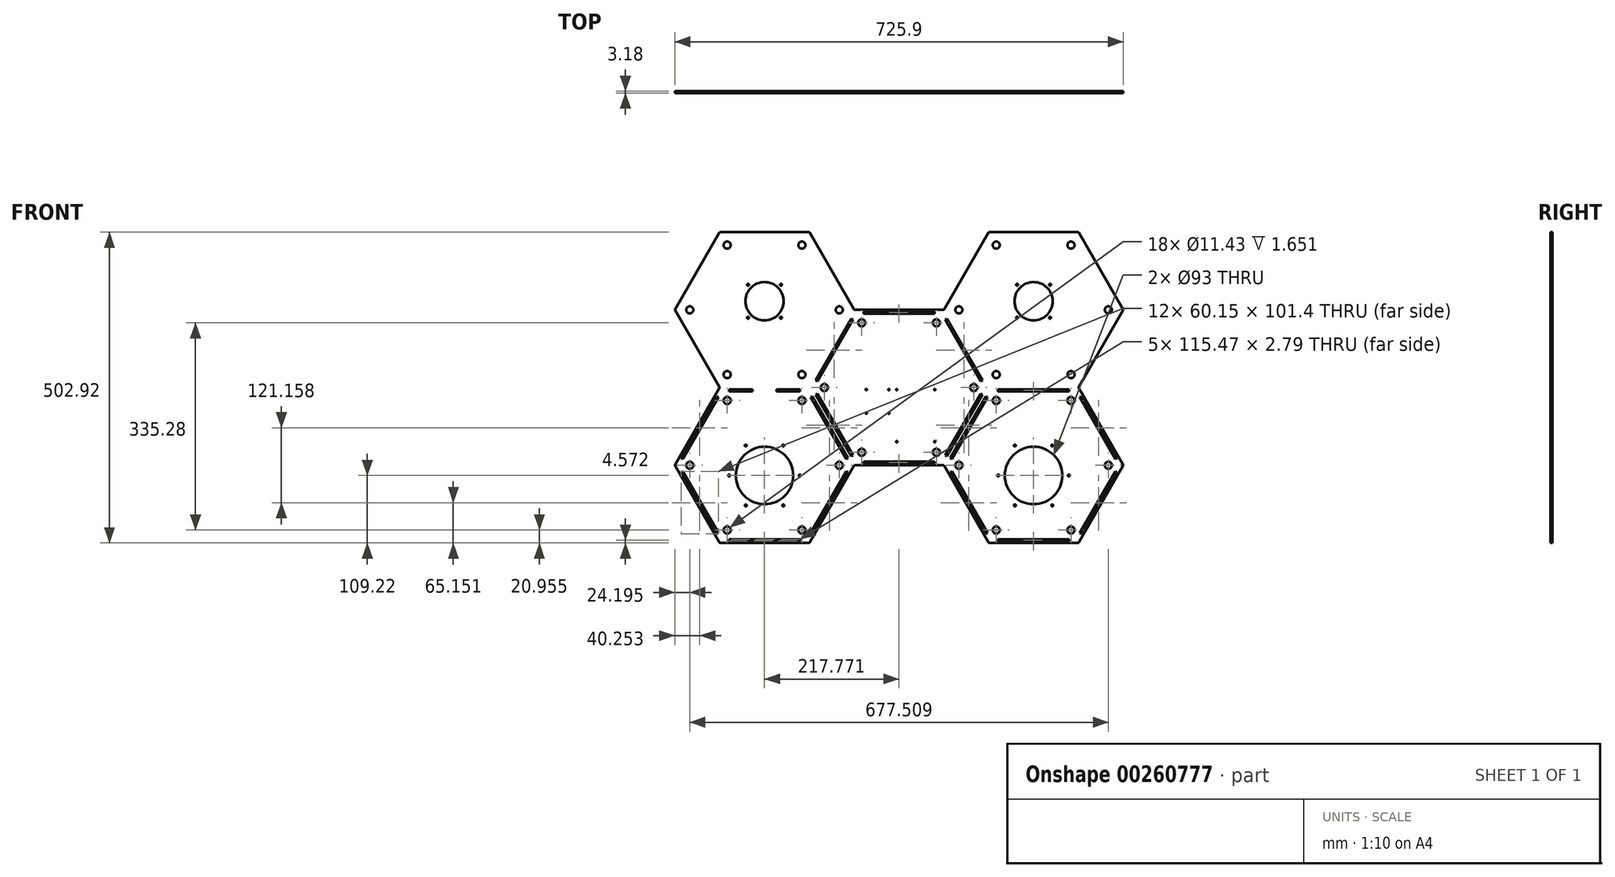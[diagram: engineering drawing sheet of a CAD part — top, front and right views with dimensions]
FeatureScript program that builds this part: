
annotation { "Feature Type Name" : "Feature", "Feature Type Description" : "" }
export const myFeature = defineFeature(function(context is Context, id is Id, definition is map)
    precondition{}
    {
        {
            var Q0;
            Q0=qCreatedBy(makeId("Front.planeOp"),FACE);
            var sketch = newSketch(context, id + "F0", { "sketchPlane" : qUnion([Q0])});
            skCircle(sketch, "E0.cCircle", {"center": v(0, 0) * mm, "radius": 125.73 * mm, "construction": true});
            skLineSegment(sketch, "E0.1", {"start": v(71.12, -125.73) * mm, "end": v(-71.12, -125.73) * mm});
            skLineSegment(sketch, "E0.4", {"start": v(-71.12, 125.73) * mm, "end": v(71.12, 125.73) * mm});
            skCircle(sketch, "E1.cCircle", {"center": v(-217.77, -125.73) * mm, "radius": 125.73 * mm, "construction": true});
            skLineSegment(sketch, "E1.0", {"start": v(-146.65, -251.46) * mm, "end": v(-288.9, -251.46) * mm});
            skLineSegment(sketch, "E1.1", {"start": v(-291.1, -250.19) * mm, "end": v(-362.22, -127) * mm});
            skLineSegment(sketch, "E1.2", {"start": v(-362.22, -124.46) * mm, "end": v(-291.1, -1.27) * mm});
            skLineSegment(sketch, "E1.5", {"start": v(-73.32, -127) * mm, "end": v(-144.45, -250.19) * mm});
            skPoint(sketch, "E1.0.midPoint", {"position": v(-217.77, -251.46) * mm});
            skCircle(sketch, "E2.cCircle", {"center": v(217.77, -125.73) * mm, "radius": 125.73 * mm, "construction": true});
            skLineSegment(sketch, "E2.0", {"start": v(362.22, -127) * mm, "end": v(291.1, -250.2) * mm});
            skLineSegment(sketch, "E2.1", {"start": v(288.9, -251.46) * mm, "end": v(146.65, -251.46) * mm});
            skLineSegment(sketch, "E2.2", {"start": v(144.45, -250.2) * mm, "end": v(73.32, -127) * mm});
            skLineSegment(sketch, "E2.5", {"start": v(291.1, -1.27) * mm, "end": v(362.22, -124.46) * mm});
            skPoint(sketch, "E2.0.midPoint", {"position": v(326.66, -188.6) * mm});
            skPoint(sketch, "E3.visualSharp", {"position": v(362.95, -125.73) * mm});
            skArc(sketch, "E3.filletArc", {"start": v(362.22, -127) * mm, "mid": v(362.56, -125.73) * mm, "end": v(362.22, -124.46) * mm});
            skPoint(sketch, "E4.visualSharp", {"position": v(290.36, -251.46) * mm});
            skArc(sketch, "E4.filletArc", {"start": v(288.9, -251.46) * mm, "mid": v(290.16, -251.12) * mm, "end": v(291.1, -250.2) * mm});
            skPoint(sketch, "E5.visualSharp", {"position": v(145.18, -251.46) * mm});
            skArc(sketch, "E5.filletArc", {"start": v(144.45, -250.2) * mm, "mid": v(145.38, -251.12) * mm, "end": v(146.65, -251.46) * mm});
            skPoint(sketch, "E6.visualSharp", {"position": v(72.6, -125.73) * mm});
            skArc(sketch, "E6.filletArc", {"start": v(73.32, -127) * mm, "mid": v(72.4, -126.07) * mm, "end": v(71.12, -125.73) * mm});
            skPoint(sketch, "E7.visualSharp", {"position": v(-72.6, -125.73) * mm});
            skArc(sketch, "E7.filletArc", {"start": v(-71.12, -125.73) * mm, "mid": v(-72.4, -126.07) * mm, "end": v(-73.32, -127) * mm});
            skPoint(sketch, "E8.visualSharp", {"position": v(-145.18, -251.46) * mm});
            skArc(sketch, "E8.filletArc", {"start": v(-146.65, -251.46) * mm, "mid": v(-145.38, -251.12) * mm, "end": v(-144.45, -250.19) * mm});
            skPoint(sketch, "E9.visualSharp", {"position": v(-290.36, -251.46) * mm});
            skArc(sketch, "E9.filletArc", {"start": v(-291.1, -250.19) * mm, "mid": v(-290.16, -251.12) * mm, "end": v(-288.9, -251.46) * mm});
            skPoint(sketch, "E10.visualSharp", {"position": v(-362.95, -125.73) * mm});
            skArc(sketch, "E10.filletArc", {"start": v(-362.22, -124.46) * mm, "mid": v(-362.56, -125.73) * mm, "end": v(-362.22, -127) * mm});
            skCircle(sketch, "E11.cCircle", {"center": v(-217.77, -125.73) * mm, "radius": 104.78 * mm, "construction": true});
            skLineSegment(sketch, "E11.0", {"start": v(-278.26, -20.95) * mm, "end": v(-157.28, -20.95) * mm, "construction": true});
            skLineSegment(sketch, "E11.1", {"start": v(-157.28, -20.95) * mm, "end": v(-96.79, -125.73) * mm, "construction": true});
            skLineSegment(sketch, "E11.2", {"start": v(-96.79, -125.73) * mm, "end": v(-157.28, -230.5) * mm, "construction": true});
            skLineSegment(sketch, "E11.3", {"start": v(-157.28, -230.5) * mm, "end": v(-278.26, -230.5) * mm, "construction": true});
            skLineSegment(sketch, "E11.4", {"start": v(-278.26, -230.5) * mm, "end": v(-338.75, -125.73) * mm, "construction": true});
            skLineSegment(sketch, "E11.5", {"start": v(-338.75, -125.73) * mm, "end": v(-278.26, -20.96) * mm, "construction": true});
            skPoint(sketch, "E11.0.midPoint", {"position": v(-217.77, -20.96) * mm});
            skCircle(sketch, "E12.cCircle", {"center": v(0, 0) * mm, "radius": 104.78 * mm, "construction": true});
            skLineSegment(sketch, "E12.0", {"start": v(60.5, 104.78) * mm, "end": v(120.98, 0) * mm, "construction": true});
            skLineSegment(sketch, "E12.1", {"start": v(120.98, 0) * mm, "end": v(60.5, -104.77) * mm, "construction": true});
            skLineSegment(sketch, "E12.2", {"start": v(60.5, -104.77) * mm, "end": v(-60.5, -104.78) * mm, "construction": true});
            skLineSegment(sketch, "E12.3", {"start": v(-60.5, -104.78) * mm, "end": v(-120.98, 0) * mm, "construction": true});
            skLineSegment(sketch, "E12.4", {"start": v(-120.98, 0) * mm, "end": v(-60.5, 104.78) * mm, "construction": true});
            skLineSegment(sketch, "E12.5", {"start": v(-60.5, 104.77) * mm, "end": v(60.5, 104.77) * mm, "construction": true});
            skPoint(sketch, "E12.0.midPoint", {"position": v(90.74, 52.39) * mm});
            skCircle(sketch, "E13.cCircle", {"center": v(217.77, -125.73) * mm, "radius": 104.78 * mm, "construction": true});
            skLineSegment(sketch, "E13.0", {"start": v(157.28, -20.96) * mm, "end": v(278.26, -20.96) * mm, "construction": true});
            skLineSegment(sketch, "E13.1", {"start": v(278.26, -20.96) * mm, "end": v(338.75, -125.73) * mm, "construction": true});
            skLineSegment(sketch, "E13.2", {"start": v(338.75, -125.73) * mm, "end": v(278.26, -230.5) * mm, "construction": true});
            skLineSegment(sketch, "E13.3", {"start": v(278.26, -230.5) * mm, "end": v(157.28, -230.5) * mm, "construction": true});
            skLineSegment(sketch, "E13.4", {"start": v(157.28, -230.5) * mm, "end": v(96.79, -125.73) * mm, "construction": true});
            skLineSegment(sketch, "E13.5", {"start": v(96.79, -125.73) * mm, "end": v(157.28, -20.96) * mm, "construction": true});
            skPoint(sketch, "E13.0.midPoint", {"position": v(217.77, -20.96) * mm});
            skCircle(sketch, "E14", {"center": v(-278.26, -20.96) * mm, "radius": 5.72 * mm});
            skCircle(sketch, "E15", {"center": v(-157.28, -20.95) * mm, "radius": 5.72 * mm});
            skCircle(sketch, "E16", {"center": v(-338.75, -125.73) * mm, "radius": 5.72 * mm});
            skCircle(sketch, "E17", {"center": v(-278.26, -230.5) * mm, "radius": 5.72 * mm});
            skCircle(sketch, "E18", {"center": v(-157.28, -230.5) * mm, "radius": 5.72 * mm});
            skCircle(sketch, "E19", {"center": v(-96.79, -125.73) * mm, "radius": 5.72 * mm});
            skCircle(sketch, "E20", {"center": v(-60.5, -104.78) * mm, "radius": 5.72 * mm});
            skCircle(sketch, "E21", {"center": v(-120.98, 0) * mm, "radius": 5.72 * mm});
            skCircle(sketch, "E22", {"center": v(-60.5, 104.77) * mm, "radius": 5.72 * mm});
            skCircle(sketch, "E23", {"center": v(60.5, 104.77) * mm, "radius": 5.72 * mm});
            skCircle(sketch, "E24", {"center": v(120.98, 0) * mm, "radius": 5.72 * mm});
            skCircle(sketch, "E25", {"center": v(60.5, -104.77) * mm, "radius": 5.72 * mm});
            skCircle(sketch, "E26", {"center": v(96.79, -125.73) * mm, "radius": 5.72 * mm});
            skCircle(sketch, "E27", {"center": v(157.28, -20.96) * mm, "radius": 5.72 * mm});
            skCircle(sketch, "E28", {"center": v(278.26, -20.96) * mm, "radius": 5.72 * mm});
            skCircle(sketch, "E29", {"center": v(338.75, -125.73) * mm, "radius": 5.72 * mm});
            skCircle(sketch, "E30", {"center": v(278.26, -230.5) * mm, "radius": 5.72 * mm});
            skCircle(sketch, "E31", {"center": v(157.28, -230.5) * mm, "radius": 5.72 * mm});
            skCircle(sketch, "E32.cCircle", {"center": v(-217.77, 125.73) * mm, "radius": 125.73 * mm, "construction": true});
            skLineSegment(sketch, "E32.0", {"start": v(-145.18, 251.46) * mm, "end": v(-73.32, 127) * mm});
            skLineSegment(sketch, "E32.3", {"start": v(-291.1, 1.27) * mm, "end": v(-362.95, 125.73) * mm});
            skLineSegment(sketch, "E32.4", {"start": v(-362.95, 125.73) * mm, "end": v(-290.36, 251.46) * mm});
            skLineSegment(sketch, "E32.5", {"start": v(-290.36, 251.46) * mm, "end": v(-145.18, 251.46) * mm});
            skPoint(sketch, "E32.0.midPoint", {"position": v(-108.89, 188.6) * mm});
            skCircle(sketch, "E33.cCircle", {"center": v(217.77, 125.73) * mm, "radius": 125.73 * mm, "construction": true});
            skLineSegment(sketch, "E33.0", {"start": v(290.36, 251.46) * mm, "end": v(362.95, 125.73) * mm});
            skLineSegment(sketch, "E33.1", {"start": v(362.95, 125.73) * mm, "end": v(291.1, 1.27) * mm});
            skLineSegment(sketch, "E33.4", {"start": v(73.32, 127) * mm, "end": v(145.18, 251.46) * mm});
            skLineSegment(sketch, "E33.5", {"start": v(145.18, 251.46) * mm, "end": v(290.36, 251.46) * mm});
            skPoint(sketch, "E33.0.midPoint", {"position": v(326.66, 188.6) * mm});
            skCircle(sketch, "E34.MirrorC", {"center": v(-278.26, 20.96) * mm, "radius": 5.72 * mm});
            skCircle(sketch, "E35.MirrorC", {"center": v(-157.28, 20.95) * mm, "radius": 5.72 * mm});
            skCircle(sketch, "E36.MirrorC", {"center": v(-338.75, 125.73) * mm, "radius": 5.72 * mm});
            skCircle(sketch, "E37.MirrorC", {"center": v(-278.26, 230.5) * mm, "radius": 5.72 * mm});
            skCircle(sketch, "E38.MirrorC", {"center": v(-157.28, 230.5) * mm, "radius": 5.72 * mm});
            skCircle(sketch, "E39.MirrorC", {"center": v(-96.79, 125.73) * mm, "radius": 5.72 * mm});
            skCircle(sketch, "E40.MirrorC", {"center": v(157.28, 20.96) * mm, "radius": 5.72 * mm});
            skCircle(sketch, "E41.MirrorC", {"center": v(278.26, 20.96) * mm, "radius": 5.72 * mm});
            skCircle(sketch, "E42.MirrorC", {"center": v(96.79, 125.73) * mm, "radius": 5.72 * mm});
            skCircle(sketch, "E43.MirrorC", {"center": v(338.75, 125.73) * mm, "radius": 5.72 * mm});
            skCircle(sketch, "E44.MirrorC", {"center": v(278.26, 230.5) * mm, "radius": 5.72 * mm});
            skCircle(sketch, "E45.MirrorC", {"center": v(157.28, 230.5) * mm, "radius": 5.72 * mm});
            skPoint(sketch, "E46.visualSharp", {"position": v(-290.36, 0) * mm});
            skArc(sketch, "E46.filletArc", {"start": v(-291.1, -1.27) * mm, "mid": v(-290.75, 0) * mm, "end": v(-291.1, 1.27) * mm});
            skPoint(sketch, "E47.visualSharp", {"position": v(290.36, 0) * mm});
            skArc(sketch, "E47.filletArc", {"start": v(291.1, 1.27) * mm, "mid": v(290.75, 0) * mm, "end": v(291.1, -1.27) * mm});
            skPoint(sketch, "E48.visualSharp", {"position": v(72.6, 125.73) * mm});
            skArc(sketch, "E48.filletArc", {"start": v(71.12, 125.73) * mm, "mid": v(72.4, 126.07) * mm, "end": v(73.32, 127) * mm});
            skPoint(sketch, "E49.visualSharp", {"position": v(-72.6, 125.73) * mm});
            skArc(sketch, "E49.filletArc", {"start": v(-73.32, 127) * mm, "mid": v(-72.4, 126.07) * mm, "end": v(-71.12, 125.73) * mm});
            skSolve(sketch);
        }
        {
            var Q0;
            Q0=makeQuery(id+"F0.imprint","IMPRINT",FACE,{"disambiguationData":[TD([[makeQuery(id+"F0.imprint","IMPRINT",EDGE,{"derivedFrom":sQuery(id+"F0.wireOp",EDGE,"E0.1")}),-1.0]])]});
            extrude(context, id + "F1", {"entities" : qUnion([Q0]), "depth" : 3.17 * mm});
        }
        {
            var Q0;
            Q0=makeQuery(id+"F0.imprint","IMPRINT",FACE,{"disambiguationData":[TD([[makeQuery(id+"F0.imprint","IMPRINT",EDGE,{"derivedFrom":sQuery(id+"F0.wireOp",EDGE,"E24")}),1.0]])]});
            var Q1;
            Q1=makeQuery(id+"F0.imprint","IMPRINT",FACE,{"disambiguationData":[TD([[makeQuery(id+"F0.imprint","IMPRINT",EDGE,{"derivedFrom":sQuery(id+"F0.wireOp",EDGE,"E27")}),1.0]])]});
            var Q2;
            Q2=makeQuery(id+"F0.imprint","IMPRINT",FACE,{"disambiguationData":[TD([[makeQuery(id+"F0.imprint","IMPRINT",EDGE,{"derivedFrom":sQuery(id+"F0.wireOp",EDGE,"E28")}),1.0]])]});
            var Q3;
            Q3=makeQuery(id+"F0.imprint","IMPRINT",FACE,{"disambiguationData":[TD([[makeQuery(id+"F0.imprint","IMPRINT",EDGE,{"derivedFrom":sQuery(id+"F0.wireOp",EDGE,"E29")}),1.0]])]});
            var Q4;
            Q4=makeQuery(id+"F0.imprint","IMPRINT",FACE,{"disambiguationData":[TD([[makeQuery(id+"F0.imprint","IMPRINT",EDGE,{"derivedFrom":sQuery(id+"F0.wireOp",EDGE,"E30")}),1.0]])]});
            var Q5;
            Q5=makeQuery(id+"F0.imprint","IMPRINT",FACE,{"disambiguationData":[TD([[makeQuery(id+"F0.imprint","IMPRINT",EDGE,{"derivedFrom":sQuery(id+"F0.wireOp",EDGE,"E31")}),1.0]])]});
            var Q6;
            Q6=makeQuery(id+"F0.imprint","IMPRINT",FACE,{"disambiguationData":[TD([[makeQuery(id+"F0.imprint","IMPRINT",EDGE,{"derivedFrom":sQuery(id+"F0.wireOp",EDGE,"E26")}),1.0]])]});
            var Q7;
            Q7=makeQuery(id+"F0.imprint","IMPRINT",FACE,{"disambiguationData":[TD([[makeQuery(id+"F0.imprint","IMPRINT",EDGE,{"derivedFrom":sQuery(id+"F0.wireOp",EDGE,"E25")}),1.0]])]});
            var Q8;
            Q8=makeQuery(id+"F0.imprint","IMPRINT",FACE,{"disambiguationData":[TD([[makeQuery(id+"F0.imprint","IMPRINT",EDGE,{"derivedFrom":sQuery(id+"F0.wireOp",EDGE,"E20")}),1.0]])]});
            var Q9;
            Q9=makeQuery(id+"F0.imprint","IMPRINT",FACE,{"disambiguationData":[TD([[makeQuery(id+"F0.imprint","IMPRINT",EDGE,{"derivedFrom":sQuery(id+"F0.wireOp",EDGE,"E19")}),1.0]])]});
            var Q10;
            Q10=makeQuery(id+"F0.imprint","IMPRINT",FACE,{"disambiguationData":[TD([[makeQuery(id+"F0.imprint","IMPRINT",EDGE,{"derivedFrom":sQuery(id+"F0.wireOp",EDGE,"E18")}),1.0]])]});
            var Q11;
            Q11=makeQuery(id+"F0.imprint","IMPRINT",FACE,{"disambiguationData":[TD([[makeQuery(id+"F0.imprint","IMPRINT",EDGE,{"derivedFrom":sQuery(id+"F0.wireOp",EDGE,"E17")}),1.0]])]});
            var Q12;
            Q12=makeQuery(id+"F0.imprint","IMPRINT",FACE,{"disambiguationData":[TD([[makeQuery(id+"F0.imprint","IMPRINT",EDGE,{"derivedFrom":sQuery(id+"F0.wireOp",EDGE,"E16")}),1.0]])]});
            var Q13;
            Q13=makeQuery(id+"F0.imprint","IMPRINT",FACE,{"disambiguationData":[TD([[makeQuery(id+"F0.imprint","IMPRINT",EDGE,{"derivedFrom":sQuery(id+"F0.wireOp",EDGE,"E14")}),1.0]])]});
            var Q14;
            Q14=makeQuery(id+"F0.imprint","IMPRINT",FACE,{"disambiguationData":[TD([[makeQuery(id+"F0.imprint","IMPRINT",EDGE,{"derivedFrom":sQuery(id+"F0.wireOp",EDGE,"E15")}),1.0]])]});
            var Q15;
            Q15=makeQuery(id+"F0.imprint","IMPRINT",FACE,{"disambiguationData":[TD([[makeQuery(id+"F0.imprint","IMPRINT",EDGE,{"derivedFrom":sQuery(id+"F0.wireOp",EDGE,"E21")}),1.0]])]});
            var Q16;
            Q16=makeQuery(id+"F0.imprint","IMPRINT",FACE,{"disambiguationData":[TD([[makeQuery(id+"F0.imprint","IMPRINT",EDGE,{"derivedFrom":sQuery(id+"F0.wireOp",EDGE,"E22")}),1.0]])]});
            var Q17;
            Q17=makeQuery(id+"F0.imprint","IMPRINT",FACE,{"disambiguationData":[TD([[makeQuery(id+"F0.imprint","IMPRINT",EDGE,{"derivedFrom":sQuery(id+"F0.wireOp",EDGE,"E23")}),1.0]])]});
            extrude(context, id + "F2", {"entities" : qUnion([Q0, Q1, Q2, Q3, Q4, Q5, Q6, Q7, Q8, Q9, Q10, Q11, Q12, Q13, Q14, Q15, Q16, Q17]), "operationType" : NewBodyOperationType.ADD, "depth" : 1.52 * mm});
        }
        {
            var Q0;
            Q0=makeQuery(id+"F1.opExtrude","CAP_FACE",FACE,{"disambiguationData":[OSD([sQuery(id+"F0.wireOp",EDGE,"E0.1"),sQuery(id+"F0.wireOp",EDGE,"E0.3"),sQuery(id+"F0.wireOp",EDGE,"E0.4"),sQuery(id+"F0.wireOp",EDGE,"E0.5"),sQuery(id+"F0.wireOp",EDGE,"E1.0"),sQuery(id+"F0.wireOp",EDGE,"E1.1"),sQuery(id+"F0.wireOp",EDGE,"E1.2"),sQuery(id+"F0.wireOp",EDGE,"E1.3"),sQuery(id+"F0.wireOp",EDGE,"E1.5"),sQuery(id+"F0.wireOp",EDGE,"E2.0"),sQuery(id+"F0.wireOp",EDGE,"E2.1"),sQuery(id+"F0.wireOp",EDGE,"E2.2"),sQuery(id+"F0.wireOp",EDGE,"E2.4"),sQuery(id+"F0.wireOp",EDGE,"E2.5"),sQuery(id+"F0.wireOp",EDGE,"d6ac2782-956d-471b-80da-3802cf03d7d4.filletArc"),sQuery(id+"F0.wireOp",EDGE,"c4cdf07e-024d-4eca-af19-9d9f9e97ded8.filletArc"),sQuery(id+"F0.wireOp",EDGE,"a3f6d1de-1ee9-4e34-8bae-e473824aa244.filletArc"),sQuery(id+"F0.wireOp",EDGE,"65f81674-14ca-4850-961e-3e155791f191.filletArc"),sQuery(id+"F0.wireOp",EDGE,"E3.filletArc"),sQuery(id+"F0.wireOp",EDGE,"E4.filletArc"),sQuery(id+"F0.wireOp",EDGE,"E5.filletArc"),sQuery(id+"F0.wireOp",EDGE,"E6.filletArc"),sQuery(id+"F0.wireOp",EDGE,"E7.filletArc"),sQuery(id+"F0.wireOp",EDGE,"E8.filletArc"),sQuery(id+"F0.wireOp",EDGE,"E9.filletArc"),sQuery(id+"F0.wireOp",EDGE,"E10.filletArc"),sQuery(id+"F0.wireOp",EDGE,"dc3c3065-ab0f-4737-a8f2-ea36e4ef4733.filletArc"),sQuery(id+"F0.wireOp",EDGE,"b4747763-c87b-4525-9a29-1839d3782590.filletArc"),sQuery(id+"F0.wireOp",EDGE,"E14"),sQuery(id+"F0.wireOp",EDGE,"E15"),sQuery(id+"F0.wireOp",EDGE,"E16"),sQuery(id+"F0.wireOp",EDGE,"E17"),sQuery(id+"F0.wireOp",EDGE,"E18"),sQuery(id+"F0.wireOp",EDGE,"E19"),sQuery(id+"F0.wireOp",EDGE,"E20"),sQuery(id+"F0.wireOp",EDGE,"E21"),sQuery(id+"F0.wireOp",EDGE,"E22"),sQuery(id+"F0.wireOp",EDGE,"E23"),sQuery(id+"F0.wireOp",EDGE,"E24"),sQuery(id+"F0.wireOp",EDGE,"E25"),sQuery(id+"F0.wireOp",EDGE,"E26"),sQuery(id+"F0.wireOp",EDGE,"E27"),sQuery(id+"F0.wireOp",EDGE,"E28"),sQuery(id+"F0.wireOp",EDGE,"E29"),sQuery(id+"F0.wireOp",EDGE,"E30"),sQuery(id+"F0.wireOp",EDGE,"E31")])],"isStart":false});
            var sketch = newSketch(context, id + "F3", { "sketchPlane" : qUnion([Q0])});
            skPoint(sketch, "E50", {"position": v(-217.77, -127) * mm});
            skCircle(sketch, "E51", {"center": v(-217.77, 139.7) * mm, "radius": 31 * mm});
            skCircle(sketch, "E52", {"center": v(-217.77, -142.24) * mm, "radius": 46.5 * mm});
            skLineSegment(sketch, "E53", {"start": v(-295.75, -142.24) * mm, "end": v(-133.33, -142.24) * mm, "construction": true});
            skCircle(sketch, "E54", {"center": v(-217.77, -142.24) * mm, "radius": 61.65 * mm, "construction": true});
            skCircle(sketch, "E55", {"center": v(-217.77, -142.24) * mm, "radius": 57.15 * mm, "construction": true});
            skCircle(sketch, "E56", {"center": v(-160.62, -142.24) * mm, "radius": 1.52 * mm});
            skLineSegment(sketch, "E57", {"start": v(-217.77, -142.24) * mm, "end": v(-217.77, 54.01) * mm, "construction": true});
            skLineSegment(sketch, "E58", {"start": v(-217.77, -142.24) * mm, "end": v(-187.49, -93.77) * mm, "construction": true});
            skLineSegment(sketch, "E59", {"start": v(-217.77, -142.24) * mm, "end": v(-187.49, -190.7) * mm, "construction": true});
            skCircle(sketch, "E60", {"center": v(-187.49, -93.77) * mm, "radius": 1.52 * mm});
            skCircle(sketch, "E61", {"center": v(-187.49, -190.7) * mm, "radius": 1.52 * mm});
            skCircle(sketch, "E62.MirrorC", {"center": v(-248.06, -93.77) * mm, "radius": 1.52 * mm});
            skCircle(sketch, "E63.MirrorC", {"center": v(-248.06, -190.7) * mm, "radius": 1.52 * mm});
            skCircle(sketch, "E64.MirrorC", {"center": v(-274.92, -142.24) * mm, "radius": 1.52 * mm});
            skCircle(sketch, "E65", {"center": v(-217.77, 139.7) * mm, "radius": 37.72 * mm, "construction": true});
            skLineSegment(sketch, "E66", {"start": v(-217.77, 139.7) * mm, "end": v(-244.44, 166.37) * mm, "construction": true});
            skCircle(sketch, "E67", {"center": v(-244.44, 166.37) * mm, "radius": 1.52 * mm});
            skCircle(sketch, "E68", {"center": v(-244.44, 113.03) * mm, "radius": 1.52 * mm});
            skCircle(sketch, "E69", {"center": v(-191.1, 113.03) * mm, "radius": 1.52 * mm});
            skCircle(sketch, "E70", {"center": v(-191.1, 166.37) * mm, "radius": 1.52 * mm});
            skLineSegment(sketch, "E71", {"start": v(-244.44, 166.37) * mm, "end": v(-191.1, 166.37) * mm, "construction": true});
            skCircle(sketch, "E72.MirrorC", {"center": v(160.62, -142.24) * mm, "radius": 1.52 * mm});
            skCircle(sketch, "E73.MirrorC", {"center": v(187.49, -190.7) * mm, "radius": 1.52 * mm});
            skCircle(sketch, "E74.MirrorC", {"center": v(248.06, -190.7) * mm, "radius": 1.52 * mm});
            skCircle(sketch, "E75.MirrorC", {"center": v(274.92, -142.24) * mm, "radius": 1.52 * mm});
            skCircle(sketch, "E76.MirrorC", {"center": v(187.49, -93.77) * mm, "radius": 1.52 * mm});
            skCircle(sketch, "E77.MirrorC", {"center": v(248.06, -93.77) * mm, "radius": 1.52 * mm});
            skCircle(sketch, "E78.MirrorC", {"center": v(217.77, -142.24) * mm, "radius": 46.5 * mm});
            skCircle(sketch, "E79.MirrorC", {"center": v(244.44, 113.03) * mm, "radius": 1.52 * mm});
            skCircle(sketch, "E80.MirrorC", {"center": v(191.1, 113.03) * mm, "radius": 1.52 * mm});
            skCircle(sketch, "E81.MirrorC", {"center": v(191.1, 166.37) * mm, "radius": 1.52 * mm});
            skCircle(sketch, "E82.MirrorC", {"center": v(217.77, 139.7) * mm, "radius": 31 * mm});
            skCircle(sketch, "E83.MirrorC", {"center": v(244.44, 166.37) * mm, "radius": 1.52 * mm});
            skSolve(sketch);
        }
        {
            var Q0;
            Q0=qSketchRegion(id+"F3",true);
            extrude(context, id + "F4", {"entities" : qUnion([Q0]), "operationType" : NewBodyOperationType.REMOVE, "endBound" : BoundingType.THROUGH_ALL, "oppositeDirection" : true, "depth" : 25.4 * mm});
        }
        {
            var Q0;
            Q0=makeQuery(id+"F1.opExtrude","CAP_FACE",FACE,{"disambiguationData":[OSD([sQuery(id+"F0.wireOp",EDGE,"E0.1"),sQuery(id+"F0.wireOp",EDGE,"E0.3"),sQuery(id+"F0.wireOp",EDGE,"E0.4"),sQuery(id+"F0.wireOp",EDGE,"E0.5"),sQuery(id+"F0.wireOp",EDGE,"E1.0"),sQuery(id+"F0.wireOp",EDGE,"E1.1"),sQuery(id+"F0.wireOp",EDGE,"E1.2"),sQuery(id+"F0.wireOp",EDGE,"E1.3"),sQuery(id+"F0.wireOp",EDGE,"E1.5"),sQuery(id+"F0.wireOp",EDGE,"E2.0"),sQuery(id+"F0.wireOp",EDGE,"E2.1"),sQuery(id+"F0.wireOp",EDGE,"E2.2"),sQuery(id+"F0.wireOp",EDGE,"E2.4"),sQuery(id+"F0.wireOp",EDGE,"E2.5"),sQuery(id+"F0.wireOp",EDGE,"d6ac2782-956d-471b-80da-3802cf03d7d4.filletArc"),sQuery(id+"F0.wireOp",EDGE,"c4cdf07e-024d-4eca-af19-9d9f9e97ded8.filletArc"),sQuery(id+"F0.wireOp",EDGE,"a3f6d1de-1ee9-4e34-8bae-e473824aa244.filletArc"),sQuery(id+"F0.wireOp",EDGE,"65f81674-14ca-4850-961e-3e155791f191.filletArc"),sQuery(id+"F0.wireOp",EDGE,"E3.filletArc"),sQuery(id+"F0.wireOp",EDGE,"E4.filletArc"),sQuery(id+"F0.wireOp",EDGE,"E5.filletArc"),sQuery(id+"F0.wireOp",EDGE,"E6.filletArc"),sQuery(id+"F0.wireOp",EDGE,"E7.filletArc"),sQuery(id+"F0.wireOp",EDGE,"E8.filletArc"),sQuery(id+"F0.wireOp",EDGE,"E9.filletArc"),sQuery(id+"F0.wireOp",EDGE,"E10.filletArc"),sQuery(id+"F0.wireOp",EDGE,"dc3c3065-ab0f-4737-a8f2-ea36e4ef4733.filletArc"),sQuery(id+"F0.wireOp",EDGE,"b4747763-c87b-4525-9a29-1839d3782590.filletArc"),sQuery(id+"F0.wireOp",EDGE,"E14"),sQuery(id+"F0.wireOp",EDGE,"E15"),sQuery(id+"F0.wireOp",EDGE,"E16"),sQuery(id+"F0.wireOp",EDGE,"E17"),sQuery(id+"F0.wireOp",EDGE,"E18"),sQuery(id+"F0.wireOp",EDGE,"E19"),sQuery(id+"F0.wireOp",EDGE,"E20"),sQuery(id+"F0.wireOp",EDGE,"E21"),sQuery(id+"F0.wireOp",EDGE,"E22"),sQuery(id+"F0.wireOp",EDGE,"E23"),sQuery(id+"F0.wireOp",EDGE,"E24"),sQuery(id+"F0.wireOp",EDGE,"E25"),sQuery(id+"F0.wireOp",EDGE,"E26"),sQuery(id+"F0.wireOp",EDGE,"E27"),sQuery(id+"F0.wireOp",EDGE,"E28"),sQuery(id+"F0.wireOp",EDGE,"E29"),sQuery(id+"F0.wireOp",EDGE,"E30"),sQuery(id+"F0.wireOp",EDGE,"E31")])],"isStart":false});
            var sketch = newSketch(context, id + "F5", { "sketchPlane" : qUnion([Q0])});
            skPoint(sketch, "E84", {"position": v(-217.77, -125.73) * mm});
            skCircle(sketch, "E85.cCircle", {"center": v(-217.77, -125.73) * mm, "radius": 125.73 * mm, "construction": true});
            skLineSegment(sketch, "E85.0", {"start": v(-275.7, 0) * mm, "end": v(-159.85, 0) * mm, "construction": true});
            skLineSegment(sketch, "E85.1", {"start": v(-137.85, -12.7) * mm, "end": v(-79.92, -113.03) * mm, "construction": true});
            skLineSegment(sketch, "E85.2", {"start": v(-79.92, -138.43) * mm, "end": v(-137.85, -238.76) * mm, "construction": true});
            skLineSegment(sketch, "E85.3", {"start": v(-159.85, -251.46) * mm, "end": v(-275.7, -251.46) * mm, "construction": true});
            skLineSegment(sketch, "E85.4", {"start": v(-297.7, -238.76) * mm, "end": v(-355.62, -138.43) * mm, "construction": true});
            skLineSegment(sketch, "E85.5", {"start": v(-355.62, -113.03) * mm, "end": v(-297.7, -12.7) * mm, "construction": true});
            skPoint(sketch, "E85.0.midPoint", {"position": v(-217.77, 0) * mm});
            skPoint(sketch, "E86.visualSharp", {"position": v(-290.36, 0) * mm});
            skArc(sketch, "E86.filletArc", {"start": v(-275.7, 0) * mm, "mid": v(-288.4, -3.4) * mm, "end": v(-297.7, -12.7) * mm, "construction": true});
            skPoint(sketch, "E87.visualSharp", {"position": v(-145.18, 0) * mm});
            skArc(sketch, "E87.filletArc", {"start": v(-137.85, -12.7) * mm, "mid": v(-147.15, -3.4) * mm, "end": v(-159.85, 0) * mm, "construction": true});
            skPoint(sketch, "E88.visualSharp", {"position": v(-72.6, -125.73) * mm});
            skArc(sketch, "E88.filletArc", {"start": v(-79.92, -138.43) * mm, "mid": v(-76.52, -125.73) * mm, "end": v(-79.92, -113.03) * mm, "construction": true});
            skPoint(sketch, "E89.visualSharp", {"position": v(-145.18, -251.46) * mm});
            skArc(sketch, "E89.filletArc", {"start": v(-159.85, -251.46) * mm, "mid": v(-147.15, -248.06) * mm, "end": v(-137.85, -238.76) * mm, "construction": true});
            skPoint(sketch, "E90.visualSharp", {"position": v(-290.36, -251.46) * mm});
            skArc(sketch, "E90.filletArc", {"start": v(-297.7, -238.76) * mm, "mid": v(-288.4, -248.06) * mm, "end": v(-275.7, -251.46) * mm, "construction": true});
            skPoint(sketch, "E91.visualSharp", {"position": v(-362.95, -125.73) * mm});
            skArc(sketch, "E91.filletArc", {"start": v(-355.62, -113.03) * mm, "mid": v(-359.02, -125.73) * mm, "end": v(-355.62, -138.43) * mm, "construction": true});
            skLineSegment(sketch, "E92.bottom", {"start": v(-275.5, -5.97) * mm, "end": v(-160.04, -5.97) * mm});
            skLineSegment(sketch, "E92.top", {"start": v(-275.5, -3.17) * mm, "end": v(-160.04, -3.17) * mm});
            skLineSegment(sketch, "E92.left", {"start": v(-275.5, -3.17) * mm, "end": v(-275.5, -5.97) * mm});
            skLineSegment(sketch, "E92.right", {"start": v(-160.04, -3.17) * mm, "end": v(-160.04, -5.97) * mm});
            skLineSegment(sketch, "E93.1.0", {"start": v(-352.77, -114.45) * mm, "end": v(-295.04, -14.45) * mm});
            skLineSegment(sketch, "E93.1.1", {"start": v(-352.77, -114.45) * mm, "end": v(-350.35, -115.85) * mm});
            skLineSegment(sketch, "E93.1.2", {"start": v(-350.35, -115.85) * mm, "end": v(-292.62, -15.85) * mm});
            skLineSegment(sketch, "E93.1.3", {"start": v(-295.04, -14.45) * mm, "end": v(-292.62, -15.85) * mm});
            skLineSegment(sketch, "E93.2.0", {"start": v(-295.04, -237) * mm, "end": v(-352.77, -137) * mm});
            skLineSegment(sketch, "E93.2.1", {"start": v(-295.04, -237) * mm, "end": v(-292.62, -235.61) * mm});
            skLineSegment(sketch, "E93.2.2", {"start": v(-292.62, -235.61) * mm, "end": v(-350.35, -135.61) * mm});
            skLineSegment(sketch, "E93.2.3", {"start": v(-352.77, -137) * mm, "end": v(-350.35, -135.61) * mm});
            skLineSegment(sketch, "E93.3.0", {"start": v(-160.04, -248.29) * mm, "end": v(-275.5, -248.29) * mm});
            skLineSegment(sketch, "E93.3.1", {"start": v(-160.04, -248.29) * mm, "end": v(-160.04, -245.5) * mm});
            skLineSegment(sketch, "E93.3.2", {"start": v(-160.04, -245.5) * mm, "end": v(-275.5, -245.5) * mm});
            skLineSegment(sketch, "E93.3.3", {"start": v(-275.5, -248.29) * mm, "end": v(-275.5, -245.5) * mm});
            skLineSegment(sketch, "E93.4.0", {"start": v(-82.77, -137) * mm, "end": v(-140.5, -237) * mm});
            skLineSegment(sketch, "E93.4.1", {"start": v(-82.77, -137) * mm, "end": v(-85.19, -135.61) * mm});
            skLineSegment(sketch, "E93.4.2", {"start": v(-85.19, -135.61) * mm, "end": v(-142.92, -235.61) * mm});
            skLineSegment(sketch, "E93.4.3", {"start": v(-140.5, -237) * mm, "end": v(-142.92, -235.61) * mm});
            skLineSegment(sketch, "E93.5.0", {"start": v(-140.5, -14.45) * mm, "end": v(-82.77, -114.45) * mm});
            skLineSegment(sketch, "E93.5.1", {"start": v(-140.5, -14.45) * mm, "end": v(-142.92, -15.85) * mm});
            skLineSegment(sketch, "E93.5.2", {"start": v(-142.92, -15.85) * mm, "end": v(-85.19, -115.85) * mm});
            skLineSegment(sketch, "E93.5.3", {"start": v(-82.77, -114.45) * mm, "end": v(-85.19, -115.85) * mm});
            skLineSegment(sketch, "E94.MirrorCS", {"start": v(140.5, -14.45) * mm, "end": v(142.92, -15.85) * mm});
            skLineSegment(sketch, "E95.MirrorCS", {"start": v(140.5, -14.45) * mm, "end": v(82.77, -114.45) * mm});
            skLineSegment(sketch, "E96.MirrorCS", {"start": v(142.92, -15.85) * mm, "end": v(85.19, -115.85) * mm});
            skLineSegment(sketch, "E97.MirrorCS", {"start": v(82.77, -114.45) * mm, "end": v(85.19, -115.85) * mm});
            skLineSegment(sketch, "E98.MirrorCS", {"start": v(82.77, -137) * mm, "end": v(85.19, -135.61) * mm});
            skLineSegment(sketch, "E99.MirrorCS", {"start": v(85.19, -135.61) * mm, "end": v(142.92, -235.61) * mm});
            skLineSegment(sketch, "E100.MirrorCS", {"start": v(82.77, -137) * mm, "end": v(140.5, -237) * mm});
            skLineSegment(sketch, "E101.MirrorCS", {"start": v(140.5, -237) * mm, "end": v(142.92, -235.61) * mm});
            skLineSegment(sketch, "E102.MirrorCS", {"start": v(160.04, -248.29) * mm, "end": v(160.04, -245.5) * mm});
            skLineSegment(sketch, "E103.MirrorCS", {"start": v(160.04, -248.29) * mm, "end": v(275.5, -248.29) * mm});
            skLineSegment(sketch, "E104.MirrorCS", {"start": v(160.04, -245.5) * mm, "end": v(275.5, -245.5) * mm});
            skLineSegment(sketch, "E105.MirrorCS", {"start": v(275.5, -248.29) * mm, "end": v(275.5, -245.5) * mm});
            skLineSegment(sketch, "E106.MirrorCS", {"start": v(295.04, -237) * mm, "end": v(292.62, -235.61) * mm});
            skLineSegment(sketch, "E107.MirrorCS", {"start": v(295.04, -237) * mm, "end": v(352.77, -137) * mm});
            skLineSegment(sketch, "E108.MirrorCS", {"start": v(292.62, -235.61) * mm, "end": v(350.35, -135.61) * mm});
            skLineSegment(sketch, "E109.MirrorCS", {"start": v(352.77, -137) * mm, "end": v(350.35, -135.61) * mm});
            skLineSegment(sketch, "E110.MirrorCS", {"start": v(352.77, -114.45) * mm, "end": v(350.35, -115.85) * mm});
            skLineSegment(sketch, "E111.MirrorCS", {"start": v(350.35, -115.85) * mm, "end": v(292.62, -15.85) * mm});
            skLineSegment(sketch, "E112.MirrorCS", {"start": v(352.77, -114.45) * mm, "end": v(295.04, -14.45) * mm});
            skLineSegment(sketch, "E113.MirrorCS", {"start": v(295.04, -14.45) * mm, "end": v(292.62, -15.85) * mm});
            skLineSegment(sketch, "E114.MirrorCS", {"start": v(275.5, -3.17) * mm, "end": v(275.5, -5.97) * mm});
            skLineSegment(sketch, "E115.MirrorCS", {"start": v(275.5, -5.97) * mm, "end": v(160.04, -5.97) * mm});
            skLineSegment(sketch, "E116.MirrorCS", {"start": v(275.5, -3.17) * mm, "end": v(160.04, -3.17) * mm});
            skLineSegment(sketch, "E117.MirrorCS", {"start": v(160.04, -3.17) * mm, "end": v(160.04, -5.97) * mm});
            skLineSegment(sketch, "E118.MirrorCS", {"start": v(57.74, -122.55) * mm, "end": v(57.74, -119.76) * mm});
            skLineSegment(sketch, "E119.MirrorCS", {"start": v(-57.74, -122.55) * mm, "end": v(57.74, -122.55) * mm});
            skLineSegment(sketch, "E120.MirrorCS", {"start": v(-57.74, -119.76) * mm, "end": v(57.74, -119.76) * mm});
            skLineSegment(sketch, "E121.MirrorCS", {"start": v(-57.74, -122.55) * mm, "end": v(-57.74, -119.76) * mm});
            skLineSegment(sketch, "E122.MirrorCS", {"start": v(-77.27, -111.28) * mm, "end": v(-74.85, -109.88) * mm});
            skLineSegment(sketch, "E123.MirrorCS", {"start": v(-132.58, -9.88) * mm, "end": v(-74.85, -109.88) * mm});
            skLineSegment(sketch, "E124.MirrorCS", {"start": v(-135, -11.28) * mm, "end": v(-77.27, -111.28) * mm});
            skLineSegment(sketch, "E125.MirrorCS", {"start": v(-135, -11.28) * mm, "end": v(-132.58, -9.88) * mm});
            skLineSegment(sketch, "E126.MirrorCS", {"start": v(-135, 11.28) * mm, "end": v(-132.58, 9.88) * mm});
            skLineSegment(sketch, "E127.MirrorCS", {"start": v(-74.85, 109.88) * mm, "end": v(-132.58, 9.88) * mm});
            skLineSegment(sketch, "E128.MirrorCS", {"start": v(-77.27, 111.28) * mm, "end": v(-135, 11.28) * mm});
            skLineSegment(sketch, "E129.MirrorCS", {"start": v(-77.27, 111.28) * mm, "end": v(-74.85, 109.88) * mm});
            skLineSegment(sketch, "E130.MirrorCS", {"start": v(-57.74, 122.56) * mm, "end": v(-57.74, 119.76) * mm});
            skLineSegment(sketch, "E131.MirrorCS", {"start": v(57.74, 119.76) * mm, "end": v(-57.74, 119.76) * mm});
            skLineSegment(sketch, "E132.MirrorCS", {"start": v(57.74, 122.56) * mm, "end": v(-57.74, 122.56) * mm});
            skLineSegment(sketch, "E133.MirrorCS", {"start": v(57.74, 122.56) * mm, "end": v(57.74, 119.76) * mm});
            skLineSegment(sketch, "E134.MirrorCS", {"start": v(77.27, 111.28) * mm, "end": v(74.85, 109.88) * mm});
            skLineSegment(sketch, "E135.MirrorCS", {"start": v(132.58, 9.88) * mm, "end": v(74.85, 109.88) * mm});
            skLineSegment(sketch, "E136.MirrorCS", {"start": v(135, 11.28) * mm, "end": v(77.27, 111.28) * mm});
            skLineSegment(sketch, "E137.MirrorCS", {"start": v(135, 11.28) * mm, "end": v(132.58, 9.88) * mm});
            skLineSegment(sketch, "E138.MirrorCS", {"start": v(135, -11.28) * mm, "end": v(132.58, -9.88) * mm});
            skLineSegment(sketch, "E139.MirrorCS", {"start": v(74.85, -109.88) * mm, "end": v(132.58, -9.88) * mm});
            skLineSegment(sketch, "E140.MirrorCS", {"start": v(77.27, -111.28) * mm, "end": v(74.85, -109.88) * mm});
            skLineSegment(sketch, "E141.MirrorCS", {"start": v(77.27, -111.28) * mm, "end": v(135, -11.28) * mm});
            skSolve(sketch);
        }
        {
            var Q0;
            Q0=qSketchRegion(id+"F5",true);
            extrude(context, id + "F6", {"entities" : qUnion([Q0]), "operationType" : NewBodyOperationType.REMOVE, "endBound" : BoundingType.THROUGH_ALL, "oppositeDirection" : true, "depth" : 25.4 * mm});
        }
        {
            var Q0;
            {var subQ0=sQuery(id+"F0.wireOp",EDGE,"E19");var subQ1=sQuery(id+"F0.wireOp",EDGE,"E14");var subQ2=sQuery(id+"F0.wireOp",EDGE,"E15");var subQ3=sQuery(id+"F0.wireOp",EDGE,"E16");var subQ4=sQuery(id+"F0.wireOp",EDGE,"E17");var subQ5=sQuery(id+"F0.wireOp",EDGE,"E18");Q0=makeQuery(id+"F0aKffUkCtTZm95_1.boolean.opBoolean","SPLIT",FACE,{"disambiguationData":[TD([makeQuery(id+"F1.opExtrude","SWEPT_FACE",FACE,{"disambiguationData":[OSD([subQ1])]})])],"derivedFrom":makeQuery(id+"F1.opExtrude","CAP_FACE",FACE,{"disambiguationData":[OSD([sQuery(id+"F0.wireOp",EDGE,"E0.1"),sQuery(id+"F0.wireOp",EDGE,"E0.3"),sQuery(id+"F0.wireOp",EDGE,"E0.4"),sQuery(id+"F0.wireOp",EDGE,"E0.5"),sQuery(id+"F0.wireOp",EDGE,"E1.0"),sQuery(id+"F0.wireOp",EDGE,"E1.1"),sQuery(id+"F0.wireOp",EDGE,"E1.2"),sQuery(id+"F0.wireOp",EDGE,"E1.3"),sQuery(id+"F0.wireOp",EDGE,"E1.5"),sQuery(id+"F0.wireOp",EDGE,"E2.0"),sQuery(id+"F0.wireOp",EDGE,"E2.1"),sQuery(id+"F0.wireOp",EDGE,"E2.2"),sQuery(id+"F0.wireOp",EDGE,"E2.4"),sQuery(id+"F0.wireOp",EDGE,"E2.5"),sQuery(id+"F0.wireOp",EDGE,"d6ac2782-956d-471b-80da-3802cf03d7d4.filletArc"),sQuery(id+"F0.wireOp",EDGE,"c4cdf07e-024d-4eca-af19-9d9f9e97ded8.filletArc"),sQuery(id+"F0.wireOp",EDGE,"a3f6d1de-1ee9-4e34-8bae-e473824aa244.filletArc"),sQuery(id+"F0.wireOp",EDGE,"65f81674-14ca-4850-961e-3e155791f191.filletArc"),sQuery(id+"F0.wireOp",EDGE,"E3.filletArc"),sQuery(id+"F0.wireOp",EDGE,"E4.filletArc"),sQuery(id+"F0.wireOp",EDGE,"E5.filletArc"),sQuery(id+"F0.wireOp",EDGE,"E6.filletArc"),sQuery(id+"F0.wireOp",EDGE,"E7.filletArc"),sQuery(id+"F0.wireOp",EDGE,"E8.filletArc"),sQuery(id+"F0.wireOp",EDGE,"E9.filletArc"),sQuery(id+"F0.wireOp",EDGE,"E10.filletArc"),sQuery(id+"F0.wireOp",EDGE,"dc3c3065-ab0f-4737-a8f2-ea36e4ef4733.filletArc"),sQuery(id+"F0.wireOp",EDGE,"b4747763-c87b-4525-9a29-1839d3782590.filletArc"),subQ1,subQ2,subQ3,subQ4,subQ5,subQ0,sQuery(id+"F0.wireOp",EDGE,"E20"),sQuery(id+"F0.wireOp",EDGE,"E21"),sQuery(id+"F0.wireOp",EDGE,"E22"),sQuery(id+"F0.wireOp",EDGE,"E23"),sQuery(id+"F0.wireOp",EDGE,"E24"),sQuery(id+"F0.wireOp",EDGE,"E25"),sQuery(id+"F0.wireOp",EDGE,"E26"),sQuery(id+"F0.wireOp",EDGE,"E27"),sQuery(id+"F0.wireOp",EDGE,"E28"),sQuery(id+"F0.wireOp",EDGE,"E29"),sQuery(id+"F0.wireOp",EDGE,"E30"),sQuery(id+"F0.wireOp",EDGE,"E31")])],"isStart":false})});}
            var sketch = newSketch(context, id + "F7", { "sketchPlane" : qUnion([Q0])});
            skLineSegment(sketch, "E142.bottom", {"start": v(-237.07, -5.97) * mm, "end": v(-198.47, -5.97) * mm});
            skLineSegment(sketch, "E142.top", {"start": v(-237.07, -3.17) * mm, "end": v(-198.47, -3.17) * mm});
            skLineSegment(sketch, "E142.left", {"start": v(-237.07, -5.97) * mm, "end": v(-237.07, -3.17) * mm});
            skLineSegment(sketch, "E142.right", {"start": v(-198.47, -5.97) * mm, "end": v(-198.47, -3.17) * mm});
            skPoint(sketch, "E143", {"position": v(-217.77, -5.97) * mm});
            skSolve(sketch);
        }
        {
            var Q0;
            Q0=qSketchRegion(id+"F7",true);
            var Q1;
            {var subQ0=sQuery(id+"F0.wireOp",EDGE,"E31");var subQ1=sQuery(id+"F0.wireOp",EDGE,"E30");var subQ2=sQuery(id+"F0.wireOp",EDGE,"E29");var subQ3=sQuery(id+"F0.wireOp",EDGE,"E28");var subQ4=sQuery(id+"F0.wireOp",EDGE,"E27");var subQ5=sQuery(id+"F0.wireOp",EDGE,"E26");var subQ6=sQuery(id+"F0.wireOp",EDGE,"E25");var subQ7=sQuery(id+"F0.wireOp",EDGE,"E24");var subQ8=sQuery(id+"F0.wireOp",EDGE,"E23");var subQ9=sQuery(id+"F0.wireOp",EDGE,"E22");var subQ10=sQuery(id+"F0.wireOp",EDGE,"E21");var subQ11=sQuery(id+"F0.wireOp",EDGE,"E20");var subQ12=sQuery(id+"F0.wireOp",EDGE,"E19");var subQ13=sQuery(id+"F0.wireOp",EDGE,"E18");var subQ14=sQuery(id+"F0.wireOp",EDGE,"E17");var subQ15=sQuery(id+"F0.wireOp",EDGE,"E16");var subQ16=sQuery(id+"F0.wireOp",EDGE,"E15");var subQ17=sQuery(id+"F0.wireOp",EDGE,"E14");Q1=makeQuery(id+"F2.boolean.opBoolean","MERGE",FACE,{"derivedFrom":[makeQuery(id+"F1.opExtrude","CAP_FACE",FACE,{"disambiguationData":[OSD([sQuery(id+"F0.wireOp",EDGE,"E0.1"),sQuery(id+"F0.wireOp",EDGE,"E0.3"),sQuery(id+"F0.wireOp",EDGE,"E0.4"),sQuery(id+"F0.wireOp",EDGE,"E0.5"),sQuery(id+"F0.wireOp",EDGE,"E1.0"),sQuery(id+"F0.wireOp",EDGE,"E1.1"),sQuery(id+"F0.wireOp",EDGE,"E1.2"),sQuery(id+"F0.wireOp",EDGE,"E1.3"),sQuery(id+"F0.wireOp",EDGE,"E1.5"),sQuery(id+"F0.wireOp",EDGE,"E2.0"),sQuery(id+"F0.wireOp",EDGE,"E2.1"),sQuery(id+"F0.wireOp",EDGE,"E2.2"),sQuery(id+"F0.wireOp",EDGE,"E2.4"),sQuery(id+"F0.wireOp",EDGE,"E2.5"),sQuery(id+"F0.wireOp",EDGE,"d6ac2782-956d-471b-80da-3802cf03d7d4.filletArc"),sQuery(id+"F0.wireOp",EDGE,"c4cdf07e-024d-4eca-af19-9d9f9e97ded8.filletArc"),sQuery(id+"F0.wireOp",EDGE,"a3f6d1de-1ee9-4e34-8bae-e473824aa244.filletArc"),sQuery(id+"F0.wireOp",EDGE,"65f81674-14ca-4850-961e-3e155791f191.filletArc"),sQuery(id+"F0.wireOp",EDGE,"E3.filletArc"),sQuery(id+"F0.wireOp",EDGE,"E4.filletArc"),sQuery(id+"F0.wireOp",EDGE,"E5.filletArc"),sQuery(id+"F0.wireOp",EDGE,"E6.filletArc"),sQuery(id+"F0.wireOp",EDGE,"E7.filletArc"),sQuery(id+"F0.wireOp",EDGE,"E8.filletArc"),sQuery(id+"F0.wireOp",EDGE,"E9.filletArc"),sQuery(id+"F0.wireOp",EDGE,"E10.filletArc"),sQuery(id+"F0.wireOp",EDGE,"dc3c3065-ab0f-4737-a8f2-ea36e4ef4733.filletArc"),sQuery(id+"F0.wireOp",EDGE,"b4747763-c87b-4525-9a29-1839d3782590.filletArc"),subQ17,subQ16,subQ15,subQ14,subQ13,subQ12,subQ11,subQ10,subQ9,subQ8,subQ7,subQ6,subQ5,subQ4,subQ3,subQ2,subQ1,subQ0])],"isStart":true}),makeQuery(id+"F2.opExtrude","CAP_FACE",FACE,{"disambiguationData":[OSD([subQ17])],"isStart":true}),makeQuery(id+"F2.opExtrude","CAP_FACE",FACE,{"disambiguationData":[OSD([subQ16])],"isStart":true}),makeQuery(id+"F2.opExtrude","CAP_FACE",FACE,{"disambiguationData":[OSD([subQ15])],"isStart":true}),makeQuery(id+"F2.opExtrude","CAP_FACE",FACE,{"disambiguationData":[OSD([subQ14])],"isStart":true}),makeQuery(id+"F2.opExtrude","CAP_FACE",FACE,{"disambiguationData":[OSD([subQ13])],"isStart":true}),makeQuery(id+"F2.opExtrude","CAP_FACE",FACE,{"disambiguationData":[OSD([subQ12])],"isStart":true}),makeQuery(id+"F2.opExtrude","CAP_FACE",FACE,{"disambiguationData":[OSD([subQ11])],"isStart":true}),makeQuery(id+"F2.opExtrude","CAP_FACE",FACE,{"disambiguationData":[OSD([subQ10])],"isStart":true}),makeQuery(id+"F2.opExtrude","CAP_FACE",FACE,{"disambiguationData":[OSD([subQ9])],"isStart":true}),makeQuery(id+"F2.opExtrude","CAP_FACE",FACE,{"disambiguationData":[OSD([subQ8])],"isStart":true}),makeQuery(id+"F2.opExtrude","CAP_FACE",FACE,{"disambiguationData":[OSD([subQ7])],"isStart":true}),makeQuery(id+"F2.opExtrude","CAP_FACE",FACE,{"disambiguationData":[OSD([subQ6])],"isStart":true}),makeQuery(id+"F2.opExtrude","CAP_FACE",FACE,{"disambiguationData":[OSD([subQ5])],"isStart":true}),makeQuery(id+"F2.opExtrude","CAP_FACE",FACE,{"disambiguationData":[OSD([subQ4])],"isStart":true}),makeQuery(id+"F2.opExtrude","CAP_FACE",FACE,{"disambiguationData":[OSD([subQ3])],"isStart":true}),makeQuery(id+"F2.opExtrude","CAP_FACE",FACE,{"disambiguationData":[OSD([subQ2])],"isStart":true}),makeQuery(id+"F2.opExtrude","CAP_FACE",FACE,{"disambiguationData":[OSD([subQ1])],"isStart":true}),makeQuery(id+"F2.opExtrude","CAP_FACE",FACE,{"disambiguationData":[OSD([subQ0])],"isStart":true})]});}
            extrude(context, id + "F8", {"entities" : qUnion([Q0]), "operationType" : NewBodyOperationType.ADD, "endBound" : BoundingType.UP_TO_SURFACE, "oppositeDirection" : true, "endBoundEntityFace" : qUnion([Q1]), "depth" : 25.4 * mm});
        }
        {
            var Q0;
            {var subQ0=sQuery(id+"F7.wireOp",EDGE,"E142.right");var subQ1=sQuery(id+"F7.wireOp",EDGE,"E142.left");var subQ2=sQuery(id+"F7.wireOp",EDGE,"E142.top");var subQ3=sQuery(id+"F7.wireOp",EDGE,"E142.bottom");var subQ4=sQuery(id+"F0.wireOp",EDGE,"E19");var subQ5=sQuery(id+"F0.wireOp",EDGE,"E14");var subQ6=sQuery(id+"F0.wireOp",EDGE,"E15");var subQ7=sQuery(id+"F0.wireOp",EDGE,"E16");var subQ8=sQuery(id+"F0.wireOp",EDGE,"E17");var subQ9=sQuery(id+"F0.wireOp",EDGE,"E18");var subQ10=sQuery(id+"F0.wireOp",EDGE,"E31");var subQ11=sQuery(id+"F0.wireOp",EDGE,"E30");var subQ12=sQuery(id+"F0.wireOp",EDGE,"E29");var subQ13=sQuery(id+"F0.wireOp",EDGE,"E28");var subQ14=sQuery(id+"F0.wireOp",EDGE,"E27");var subQ15=sQuery(id+"F0.wireOp",EDGE,"E26");var subQ16=sQuery(id+"F0.wireOp",EDGE,"E25");var subQ17=sQuery(id+"F0.wireOp",EDGE,"E24");var subQ18=sQuery(id+"F0.wireOp",EDGE,"E23");var subQ19=sQuery(id+"F0.wireOp",EDGE,"E22");var subQ20=sQuery(id+"F0.wireOp",EDGE,"E21");var subQ21=sQuery(id+"F0.wireOp",EDGE,"E20");var subQ22=sQuery(id+"F0.wireOp",EDGE,"b4747763-c87b-4525-9a29-1839d3782590.filletArc");var subQ23=sQuery(id+"F0.wireOp",EDGE,"dc3c3065-ab0f-4737-a8f2-ea36e4ef4733.filletArc");var subQ24=sQuery(id+"F0.wireOp",EDGE,"E10.filletArc");var subQ25=sQuery(id+"F0.wireOp",EDGE,"E9.filletArc");var subQ26=sQuery(id+"F0.wireOp",EDGE,"E8.filletArc");var subQ27=sQuery(id+"F0.wireOp",EDGE,"E7.filletArc");var subQ28=sQuery(id+"F0.wireOp",EDGE,"E6.filletArc");var subQ29=sQuery(id+"F0.wireOp",EDGE,"E5.filletArc");var subQ30=sQuery(id+"F0.wireOp",EDGE,"E4.filletArc");var subQ31=sQuery(id+"F0.wireOp",EDGE,"E3.filletArc");var subQ32=sQuery(id+"F0.wireOp",EDGE,"65f81674-14ca-4850-961e-3e155791f191.filletArc");var subQ33=sQuery(id+"F0.wireOp",EDGE,"a3f6d1de-1ee9-4e34-8bae-e473824aa244.filletArc");var subQ34=sQuery(id+"F0.wireOp",EDGE,"c4cdf07e-024d-4eca-af19-9d9f9e97ded8.filletArc");var subQ35=sQuery(id+"F0.wireOp",EDGE,"d6ac2782-956d-471b-80da-3802cf03d7d4.filletArc");var subQ36=sQuery(id+"F0.wireOp",EDGE,"E2.5");var subQ37=sQuery(id+"F0.wireOp",EDGE,"E2.4");var subQ38=sQuery(id+"F0.wireOp",EDGE,"E2.2");var subQ39=sQuery(id+"F0.wireOp",EDGE,"E2.1");var subQ40=sQuery(id+"F0.wireOp",EDGE,"E2.0");var subQ41=sQuery(id+"F0.wireOp",EDGE,"E1.5");var subQ42=sQuery(id+"F0.wireOp",EDGE,"E1.3");var subQ43=sQuery(id+"F0.wireOp",EDGE,"E1.2");var subQ44=sQuery(id+"F0.wireOp",EDGE,"E1.1");var subQ45=sQuery(id+"F0.wireOp",EDGE,"E1.0");var subQ46=sQuery(id+"F0.wireOp",EDGE,"E0.5");var subQ47=sQuery(id+"F0.wireOp",EDGE,"E0.4");var subQ48=sQuery(id+"F0.wireOp",EDGE,"E0.3");var subQ49=sQuery(id+"F0.wireOp",EDGE,"E0.1");var subQ50=makeQuery(id+"F1.opExtrude","CAP_FACE",FACE,{"disambiguationData":[OSD([subQ49,subQ48,subQ47,subQ46,subQ45,subQ44,subQ43,subQ42,subQ41,subQ40,subQ39,subQ38,subQ37,subQ36,subQ35,subQ34,subQ33,subQ32,subQ31,subQ30,subQ29,subQ28,subQ27,subQ26,subQ25,subQ24,subQ23,subQ22,subQ5,subQ6,subQ7,subQ8,subQ9,subQ4,subQ21,subQ20,subQ19,subQ18,subQ17,subQ16,subQ15,subQ14,subQ13,subQ12,subQ11,subQ10])],"isStart":false});Q0=makeQuery(id+"FArHMtP67R58qOK_1.1.FbB5umPfR1j8SLP_1.5.F8.boolean.opBoolean","MERGE",FACE,{"derivedFrom":[makeQuery(id+"FArHMtP67R58qOK_1.1.FbB5umPfR1j8SLP_1.4.F8.boolean.opBoolean","MERGE",FACE,{"derivedFrom":[makeQuery(id+"FArHMtP67R58qOK_1.1.FbB5umPfR1j8SLP_1.3.F8.boolean.opBoolean","MERGE",FACE,{"derivedFrom":[makeQuery(id+"FArHMtP67R58qOK_1.1.FbB5umPfR1j8SLP_1.2.F8.boolean.opBoolean","MERGE",FACE,{"derivedFrom":[makeQuery(id+"FArHMtP67R58qOK_1.1.FbB5umPfR1j8SLP_1.1.F8.boolean.opBoolean","MERGE",FACE,{"derivedFrom":[makeQuery(id+"FArHMtP67R58qOK_1.1.F8.boolean.opBoolean","MERGE",FACE,{"derivedFrom":[makeQuery(id+"F0aKffUkCtTZm95_1.boolean.opBoolean","SPLIT",FACE,{"disambiguationData":[TD([makeQuery(id+"F1.opExtrude","SWEPT_FACE",FACE,{"disambiguationData":[OSD([subQ21])]})])],"derivedFrom":subQ50}),makeQuery(id+"FZtU8A5xYbT4ezZ_1.1.FbB5umPfR1j8SLP_1.5.F8.boolean.opBoolean","MERGE",FACE,{"derivedFrom":[makeQuery(id+"FZtU8A5xYbT4ezZ_1.1.FbB5umPfR1j8SLP_1.4.F8.boolean.opBoolean","MERGE",FACE,{"derivedFrom":[makeQuery(id+"FZtU8A5xYbT4ezZ_1.1.FbB5umPfR1j8SLP_1.3.F8.boolean.opBoolean","MERGE",FACE,{"derivedFrom":[makeQuery(id+"FZtU8A5xYbT4ezZ_1.1.FbB5umPfR1j8SLP_1.2.F8.boolean.opBoolean","MERGE",FACE,{"derivedFrom":[makeQuery(id+"FZtU8A5xYbT4ezZ_1.1.FbB5umPfR1j8SLP_1.1.F8.boolean.opBoolean","MERGE",FACE,{"derivedFrom":[makeQuery(id+"FZtU8A5xYbT4ezZ_1.1.F8.boolean.opBoolean","MERGE",FACE,{"derivedFrom":[makeQuery(id+"F0aKffUkCtTZm95_1.boolean.opBoolean","SPLIT",FACE,{"disambiguationData":[TD([makeQuery(id+"F1.opExtrude","SWEPT_FACE",FACE,{"disambiguationData":[OSD([subQ15])]})])],"derivedFrom":subQ50}),makeQuery(id+"FbB5umPfR1j8SLP_1.5.F8.boolean.opBoolean","MERGE",FACE,{"derivedFrom":[makeQuery(id+"FbB5umPfR1j8SLP_1.4.F8.boolean.opBoolean","MERGE",FACE,{"derivedFrom":[makeQuery(id+"FbB5umPfR1j8SLP_1.3.F8.boolean.opBoolean","MERGE",FACE,{"derivedFrom":[makeQuery(id+"FbB5umPfR1j8SLP_1.2.F8.boolean.opBoolean","MERGE",FACE,{"derivedFrom":[makeQuery(id+"FbB5umPfR1j8SLP_1.1.F8.boolean.opBoolean","MERGE",FACE,{"derivedFrom":[makeQuery(id+"F8.boolean.opBoolean","MERGE",FACE,{"derivedFrom":[makeQuery(id+"F0aKffUkCtTZm95_1.boolean.opBoolean","SPLIT",FACE,{"disambiguationData":[TD([makeQuery(id+"F1.opExtrude","SWEPT_FACE",FACE,{"disambiguationData":[OSD([subQ49])]})])],"derivedFrom":subQ50}),makeQuery(id+"F0aKffUkCtTZm95_1.boolean.opBoolean","SPLIT",FACE,{"disambiguationData":[TD([makeQuery(id+"F1.opExtrude","SWEPT_FACE",FACE,{"disambiguationData":[OSD([subQ5])]})])],"derivedFrom":subQ50}),makeQuery(id+"F8.opExtrude","CAP_FACE",FACE,{"disambiguationData":[OSD([subQ3,subQ2,subQ1,subQ0])],"isStart":true})]}),makeQuery(id+"FbB5umPfR1j8SLP_1.1.F8.opExtrude","CAP_FACE",FACE,{"disambiguationData":[OSD([subQ3,subQ2,subQ1,subQ0])],"isStart":true})]}),makeQuery(id+"FbB5umPfR1j8SLP_1.2.F8.opExtrude","CAP_FACE",FACE,{"disambiguationData":[OSD([subQ3,subQ2,subQ1,subQ0])],"isStart":true})]}),makeQuery(id+"FbB5umPfR1j8SLP_1.3.F8.opExtrude","CAP_FACE",FACE,{"disambiguationData":[OSD([subQ3,subQ2,subQ1,subQ0])],"isStart":true})]}),makeQuery(id+"FbB5umPfR1j8SLP_1.4.F8.opExtrude","CAP_FACE",FACE,{"disambiguationData":[OSD([subQ3,subQ2,subQ1,subQ0])],"isStart":true})]}),makeQuery(id+"FbB5umPfR1j8SLP_1.5.F8.opExtrude","CAP_FACE",FACE,{"disambiguationData":[OSD([subQ3,subQ2,subQ1,subQ0])],"isStart":true})]}),makeQuery(id+"FZtU8A5xYbT4ezZ_1.1.F8.opExtrude","CAP_FACE",FACE,{"disambiguationData":[OSD([subQ3,subQ2,subQ1,subQ0])],"isStart":true})]}),makeQuery(id+"FZtU8A5xYbT4ezZ_1.1.FbB5umPfR1j8SLP_1.1.F8.opExtrude","CAP_FACE",FACE,{"disambiguationData":[OSD([subQ3,subQ2,subQ1,subQ0])],"isStart":true})]}),makeQuery(id+"FZtU8A5xYbT4ezZ_1.1.FbB5umPfR1j8SLP_1.2.F8.opExtrude","CAP_FACE",FACE,{"disambiguationData":[OSD([subQ3,subQ2,subQ1,subQ0])],"isStart":true})]}),makeQuery(id+"FZtU8A5xYbT4ezZ_1.1.FbB5umPfR1j8SLP_1.3.F8.opExtrude","CAP_FACE",FACE,{"disambiguationData":[OSD([subQ3,subQ2,subQ1,subQ0])],"isStart":true})]}),makeQuery(id+"FZtU8A5xYbT4ezZ_1.1.FbB5umPfR1j8SLP_1.4.F8.opExtrude","CAP_FACE",FACE,{"disambiguationData":[OSD([subQ3,subQ2,subQ1,subQ0])],"isStart":true})]}),makeQuery(id+"FZtU8A5xYbT4ezZ_1.1.FbB5umPfR1j8SLP_1.5.F8.opExtrude","CAP_FACE",FACE,{"disambiguationData":[OSD([subQ3,subQ2,subQ1,subQ0])],"isStart":true})]}),makeQuery(id+"FArHMtP67R58qOK_1.1.F8.opExtrude","CAP_FACE",FACE,{"disambiguationData":[OSD([subQ3,subQ2,subQ1,subQ0])],"isStart":true})]}),makeQuery(id+"FArHMtP67R58qOK_1.1.FbB5umPfR1j8SLP_1.1.F8.opExtrude","CAP_FACE",FACE,{"disambiguationData":[OSD([subQ3,subQ2,subQ1,subQ0])],"isStart":true})]}),makeQuery(id+"FArHMtP67R58qOK_1.1.FbB5umPfR1j8SLP_1.2.F8.opExtrude","CAP_FACE",FACE,{"disambiguationData":[OSD([subQ3,subQ2,subQ1,subQ0])],"isStart":true})]}),makeQuery(id+"FArHMtP67R58qOK_1.1.FbB5umPfR1j8SLP_1.3.F8.opExtrude","CAP_FACE",FACE,{"disambiguationData":[OSD([subQ3,subQ2,subQ1,subQ0])],"isStart":true})]}),makeQuery(id+"FArHMtP67R58qOK_1.1.FbB5umPfR1j8SLP_1.4.F8.opExtrude","CAP_FACE",FACE,{"disambiguationData":[OSD([subQ3,subQ2,subQ1,subQ0])],"isStart":true})]}),makeQuery(id+"FArHMtP67R58qOK_1.1.FbB5umPfR1j8SLP_1.5.F8.opExtrude","CAP_FACE",FACE,{"disambiguationData":[OSD([subQ3,subQ2,subQ1,subQ0])],"isStart":true})]});}
            var sketch = newSketch(context, id + "F9", { "sketchPlane" : qUnion([Q0])});
            skLineSegment(sketch, "E144.bottom", {"start": v(-3.73, -87.63) * mm, "end": v(57.74, -87.63) * mm, "construction": true});
            skLineSegment(sketch, "E144.top", {"start": v(-3.73, -3.3) * mm, "end": v(57.74, -3.3) * mm, "construction": true});
            skLineSegment(sketch, "E144.left", {"start": v(-3.73, -87.63) * mm, "end": v(-3.73, -3.3) * mm, "construction": true});
            skLineSegment(sketch, "E144.right", {"start": v(57.74, -87.63) * mm, "end": v(57.74, -3.3) * mm, "construction": true});
            skLineSegment(sketch, "E145.bottom", {"start": v(-53, -3.3) * mm, "end": v(-16.43, -3.3) * mm, "construction": true});
            skLineSegment(sketch, "E145.top", {"start": v(-53, -41.4) * mm, "end": v(-16.43, -41.4) * mm, "construction": true});
            skLineSegment(sketch, "E145.left", {"start": v(-53, -3.3) * mm, "end": v(-53, -41.4) * mm, "construction": true});
            skLineSegment(sketch, "E145.right", {"start": v(-16.43, -3.3) * mm, "end": v(-16.43, -41.4) * mm, "construction": true});
            skCircle(sketch, "E146", {"center": v(-53, -3.3) * mm, "radius": 1.14 * mm});
            skCircle(sketch, "E147", {"center": v(-16.43, -3.3) * mm, "radius": 1.14 * mm});
            skCircle(sketch, "E148", {"center": v(-53, -41.4) * mm, "radius": 1.14 * mm});
            skCircle(sketch, "E149", {"center": v(-3.73, -87.63) * mm, "radius": 1.14 * mm});
            skCircle(sketch, "E150", {"center": v(57.74, -87.63) * mm, "radius": 1.14 * mm});
            skCircle(sketch, "E151", {"center": v(57.74, -3.3) * mm, "radius": 1.14 * mm});
            skCircle(sketch, "E152", {"center": v(-3.73, -3.3) * mm, "radius": 1.14 * mm});
            skCircle(sketch, "E153", {"center": v(-16.43, -41.4) * mm, "radius": 1.14 * mm});
            skSolve(sketch);
        }
        {
            var Q0;
            Q0=qSketchRegion(id+"F9",true);
            var Q1;
            {var subQ0=sQuery(id+"F0.wireOp",EDGE,"E31");var subQ1=sQuery(id+"F0.wireOp",EDGE,"E30");var subQ2=sQuery(id+"F0.wireOp",EDGE,"E29");var subQ3=sQuery(id+"F0.wireOp",EDGE,"E28");var subQ4=sQuery(id+"F0.wireOp",EDGE,"E27");var subQ5=sQuery(id+"F0.wireOp",EDGE,"E26");var subQ6=sQuery(id+"F0.wireOp",EDGE,"E25");var subQ7=sQuery(id+"F0.wireOp",EDGE,"E24");var subQ8=sQuery(id+"F0.wireOp",EDGE,"E23");var subQ9=sQuery(id+"F0.wireOp",EDGE,"E22");var subQ10=sQuery(id+"F0.wireOp",EDGE,"E21");var subQ11=sQuery(id+"F0.wireOp",EDGE,"E20");var subQ12=sQuery(id+"F0.wireOp",EDGE,"E19");var subQ13=sQuery(id+"F0.wireOp",EDGE,"E18");var subQ14=sQuery(id+"F0.wireOp",EDGE,"E17");var subQ15=sQuery(id+"F0.wireOp",EDGE,"E16");var subQ16=sQuery(id+"F0.wireOp",EDGE,"E15");var subQ17=sQuery(id+"F0.wireOp",EDGE,"E14");var subQ18=sQuery(id+"F0.wireOp",EDGE,"b4747763-c87b-4525-9a29-1839d3782590.filletArc");var subQ19=sQuery(id+"F0.wireOp",EDGE,"dc3c3065-ab0f-4737-a8f2-ea36e4ef4733.filletArc");var subQ20=sQuery(id+"F0.wireOp",EDGE,"E10.filletArc");var subQ21=sQuery(id+"F0.wireOp",EDGE,"E9.filletArc");var subQ22=sQuery(id+"F0.wireOp",EDGE,"E8.filletArc");var subQ23=sQuery(id+"F0.wireOp",EDGE,"E7.filletArc");var subQ24=sQuery(id+"F0.wireOp",EDGE,"E6.filletArc");var subQ25=sQuery(id+"F0.wireOp",EDGE,"E5.filletArc");var subQ26=sQuery(id+"F0.wireOp",EDGE,"E4.filletArc");var subQ27=sQuery(id+"F0.wireOp",EDGE,"E3.filletArc");var subQ28=sQuery(id+"F0.wireOp",EDGE,"65f81674-14ca-4850-961e-3e155791f191.filletArc");var subQ29=sQuery(id+"F0.wireOp",EDGE,"a3f6d1de-1ee9-4e34-8bae-e473824aa244.filletArc");var subQ30=sQuery(id+"F0.wireOp",EDGE,"c4cdf07e-024d-4eca-af19-9d9f9e97ded8.filletArc");var subQ31=sQuery(id+"F0.wireOp",EDGE,"d6ac2782-956d-471b-80da-3802cf03d7d4.filletArc");var subQ32=sQuery(id+"F0.wireOp",EDGE,"E2.5");var subQ33=sQuery(id+"F0.wireOp",EDGE,"E2.4");var subQ34=sQuery(id+"F0.wireOp",EDGE,"E2.2");var subQ35=sQuery(id+"F0.wireOp",EDGE,"E2.1");var subQ36=sQuery(id+"F0.wireOp",EDGE,"E2.0");var subQ37=sQuery(id+"F0.wireOp",EDGE,"E1.5");var subQ38=sQuery(id+"F0.wireOp",EDGE,"E1.3");var subQ39=sQuery(id+"F0.wireOp",EDGE,"E1.2");var subQ40=sQuery(id+"F0.wireOp",EDGE,"E1.1");var subQ41=sQuery(id+"F0.wireOp",EDGE,"E1.0");var subQ42=sQuery(id+"F0.wireOp",EDGE,"E0.5");var subQ43=sQuery(id+"F0.wireOp",EDGE,"E0.4");var subQ44=sQuery(id+"F0.wireOp",EDGE,"E0.3");var subQ45=sQuery(id+"F0.wireOp",EDGE,"E0.1");Q1=makeQuery(id+"FArHMtP67R58qOK_1.1.FbB5umPfR1j8SLP_1.5.F8.boolean.opBoolean","MERGE",FACE,{"derivedFrom":[makeQuery(id+"FArHMtP67R58qOK_1.1.FbB5umPfR1j8SLP_1.4.F8.boolean.opBoolean","MERGE",FACE,{"derivedFrom":[makeQuery(id+"FArHMtP67R58qOK_1.1.FbB5umPfR1j8SLP_1.3.F8.boolean.opBoolean","MERGE",FACE,{"derivedFrom":[makeQuery(id+"FArHMtP67R58qOK_1.1.FbB5umPfR1j8SLP_1.2.F8.boolean.opBoolean","MERGE",FACE,{"derivedFrom":[makeQuery(id+"FArHMtP67R58qOK_1.1.FbB5umPfR1j8SLP_1.1.F8.boolean.opBoolean","MERGE",FACE,{"derivedFrom":[makeQuery(id+"FArHMtP67R58qOK_1.1.F8.boolean.opBoolean","MERGE",FACE,{"derivedFrom":[makeQuery(id+"FZtU8A5xYbT4ezZ_1.1.FbB5umPfR1j8SLP_1.5.F8.boolean.opBoolean","MERGE",FACE,{"derivedFrom":[makeQuery(id+"FZtU8A5xYbT4ezZ_1.1.FbB5umPfR1j8SLP_1.4.F8.boolean.opBoolean","MERGE",FACE,{"derivedFrom":[makeQuery(id+"FZtU8A5xYbT4ezZ_1.1.FbB5umPfR1j8SLP_1.3.F8.boolean.opBoolean","MERGE",FACE,{"derivedFrom":[makeQuery(id+"FZtU8A5xYbT4ezZ_1.1.FbB5umPfR1j8SLP_1.2.F8.boolean.opBoolean","MERGE",FACE,{"derivedFrom":[makeQuery(id+"FZtU8A5xYbT4ezZ_1.1.FbB5umPfR1j8SLP_1.1.F8.boolean.opBoolean","MERGE",FACE,{"derivedFrom":[makeQuery(id+"FZtU8A5xYbT4ezZ_1.1.F8.boolean.opBoolean","MERGE",FACE,{"derivedFrom":[makeQuery(id+"FbB5umPfR1j8SLP_1.5.F8.boolean.opBoolean","MERGE",FACE,{"derivedFrom":[makeQuery(id+"FbB5umPfR1j8SLP_1.4.F8.boolean.opBoolean","MERGE",FACE,{"derivedFrom":[makeQuery(id+"FbB5umPfR1j8SLP_1.3.F8.boolean.opBoolean","MERGE",FACE,{"derivedFrom":[makeQuery(id+"FbB5umPfR1j8SLP_1.2.F8.boolean.opBoolean","MERGE",FACE,{"derivedFrom":[makeQuery(id+"FbB5umPfR1j8SLP_1.1.F8.boolean.opBoolean","MERGE",FACE,{"derivedFrom":[makeQuery(id+"F8.boolean.opBoolean","MERGE",FACE,{"derivedFrom":[makeQuery(id+"F2.boolean.opBoolean","MERGE",FACE,{"derivedFrom":[makeQuery(id+"F1.opExtrude","CAP_FACE",FACE,{"disambiguationData":[OSD([subQ45,subQ44,subQ43,subQ42,subQ41,subQ40,subQ39,subQ38,subQ37,subQ36,subQ35,subQ34,subQ33,subQ32,subQ31,subQ30,subQ29,subQ28,subQ27,subQ26,subQ25,subQ24,subQ23,subQ22,subQ21,subQ20,subQ19,subQ18,subQ17,subQ16,subQ15,subQ14,subQ13,subQ12,subQ11,subQ10,subQ9,subQ8,subQ7,subQ6,subQ5,subQ4,subQ3,subQ2,subQ1,subQ0])],"isStart":true}),makeQuery(id+"F2.opExtrude","CAP_FACE",FACE,{"disambiguationData":[OSD([subQ17])],"isStart":true}),makeQuery(id+"F2.opExtrude","CAP_FACE",FACE,{"disambiguationData":[OSD([subQ16])],"isStart":true}),makeQuery(id+"F2.opExtrude","CAP_FACE",FACE,{"disambiguationData":[OSD([subQ15])],"isStart":true}),makeQuery(id+"F2.opExtrude","CAP_FACE",FACE,{"disambiguationData":[OSD([subQ14])],"isStart":true}),makeQuery(id+"F2.opExtrude","CAP_FACE",FACE,{"disambiguationData":[OSD([subQ13])],"isStart":true}),makeQuery(id+"F2.opExtrude","CAP_FACE",FACE,{"disambiguationData":[OSD([subQ12])],"isStart":true}),makeQuery(id+"F2.opExtrude","CAP_FACE",FACE,{"disambiguationData":[OSD([subQ11])],"isStart":true}),makeQuery(id+"F2.opExtrude","CAP_FACE",FACE,{"disambiguationData":[OSD([subQ10])],"isStart":true}),makeQuery(id+"F2.opExtrude","CAP_FACE",FACE,{"disambiguationData":[OSD([subQ9])],"isStart":true}),makeQuery(id+"F2.opExtrude","CAP_FACE",FACE,{"disambiguationData":[OSD([subQ8])],"isStart":true}),makeQuery(id+"F2.opExtrude","CAP_FACE",FACE,{"disambiguationData":[OSD([subQ7])],"isStart":true}),makeQuery(id+"F2.opExtrude","CAP_FACE",FACE,{"disambiguationData":[OSD([subQ6])],"isStart":true}),makeQuery(id+"F2.opExtrude","CAP_FACE",FACE,{"disambiguationData":[OSD([subQ5])],"isStart":true}),makeQuery(id+"F2.opExtrude","CAP_FACE",FACE,{"disambiguationData":[OSD([subQ4])],"isStart":true}),makeQuery(id+"F2.opExtrude","CAP_FACE",FACE,{"disambiguationData":[OSD([subQ3])],"isStart":true}),makeQuery(id+"F2.opExtrude","CAP_FACE",FACE,{"disambiguationData":[OSD([subQ2])],"isStart":true}),makeQuery(id+"F2.opExtrude","CAP_FACE",FACE,{"disambiguationData":[OSD([subQ1])],"isStart":true}),makeQuery(id+"F2.opExtrude","CAP_FACE",FACE,{"disambiguationData":[OSD([subQ0])],"isStart":true})]}),makeQuery(id+"F8.opExtrude","CAP_FACE",FACE,{"disambiguationData":[OSD([subQ45,subQ44,subQ43,subQ42,subQ41,subQ40,subQ39,subQ38,subQ37,subQ36,subQ35,subQ34,subQ33,subQ32,subQ31,subQ30,subQ29,subQ28,subQ27,subQ26,subQ25,subQ24,subQ23,subQ22,subQ21,subQ20,subQ19,subQ18,subQ17,subQ16,subQ15,subQ14,subQ13,subQ12,subQ11,subQ10,subQ9,subQ8,subQ7,subQ6,subQ5,subQ4,subQ3,subQ2,subQ1,subQ0])],"isStart":false})]}),makeQuery(id+"FbB5umPfR1j8SLP_1.1.F8.opExtrude","CAP_FACE",FACE,{"disambiguationData":[OSD([subQ45,subQ44,subQ43,subQ42,subQ41,subQ40,subQ39,subQ38,subQ37,subQ36,subQ35,subQ34,subQ33,subQ32,subQ31,subQ30,subQ29,subQ28,subQ27,subQ26,subQ25,subQ24,subQ23,subQ22,subQ21,subQ20,subQ19,subQ18,subQ17,subQ16,subQ15,subQ14,subQ13,subQ12,subQ11,subQ10,subQ9,subQ8,subQ7,subQ6,subQ5,subQ4,subQ3,subQ2,subQ1,subQ0])],"isStart":false})]}),makeQuery(id+"FbB5umPfR1j8SLP_1.2.F8.opExtrude","CAP_FACE",FACE,{"disambiguationData":[OSD([subQ45,subQ44,subQ43,subQ42,subQ41,subQ40,subQ39,subQ38,subQ37,subQ36,subQ35,subQ34,subQ33,subQ32,subQ31,subQ30,subQ29,subQ28,subQ27,subQ26,subQ25,subQ24,subQ23,subQ22,subQ21,subQ20,subQ19,subQ18,subQ17,subQ16,subQ15,subQ14,subQ13,subQ12,subQ11,subQ10,subQ9,subQ8,subQ7,subQ6,subQ5,subQ4,subQ3,subQ2,subQ1,subQ0])],"isStart":false})]}),makeQuery(id+"FbB5umPfR1j8SLP_1.3.F8.opExtrude","CAP_FACE",FACE,{"disambiguationData":[OSD([subQ45,subQ44,subQ43,subQ42,subQ41,subQ40,subQ39,subQ38,subQ37,subQ36,subQ35,subQ34,subQ33,subQ32,subQ31,subQ30,subQ29,subQ28,subQ27,subQ26,subQ25,subQ24,subQ23,subQ22,subQ21,subQ20,subQ19,subQ18,subQ17,subQ16,subQ15,subQ14,subQ13,subQ12,subQ11,subQ10,subQ9,subQ8,subQ7,subQ6,subQ5,subQ4,subQ3,subQ2,subQ1,subQ0])],"isStart":false})]}),makeQuery(id+"FbB5umPfR1j8SLP_1.4.F8.opExtrude","CAP_FACE",FACE,{"disambiguationData":[OSD([subQ45,subQ44,subQ43,subQ42,subQ41,subQ40,subQ39,subQ38,subQ37,subQ36,subQ35,subQ34,subQ33,subQ32,subQ31,subQ30,subQ29,subQ28,subQ27,subQ26,subQ25,subQ24,subQ23,subQ22,subQ21,subQ20,subQ19,subQ18,subQ17,subQ16,subQ15,subQ14,subQ13,subQ12,subQ11,subQ10,subQ9,subQ8,subQ7,subQ6,subQ5,subQ4,subQ3,subQ2,subQ1,subQ0])],"isStart":false})]}),makeQuery(id+"FbB5umPfR1j8SLP_1.5.F8.opExtrude","CAP_FACE",FACE,{"disambiguationData":[OSD([subQ45,subQ44,subQ43,subQ42,subQ41,subQ40,subQ39,subQ38,subQ37,subQ36,subQ35,subQ34,subQ33,subQ32,subQ31,subQ30,subQ29,subQ28,subQ27,subQ26,subQ25,subQ24,subQ23,subQ22,subQ21,subQ20,subQ19,subQ18,subQ17,subQ16,subQ15,subQ14,subQ13,subQ12,subQ11,subQ10,subQ9,subQ8,subQ7,subQ6,subQ5,subQ4,subQ3,subQ2,subQ1,subQ0])],"isStart":false})]}),makeQuery(id+"FZtU8A5xYbT4ezZ_1.1.F8.opExtrude","CAP_FACE",FACE,{"disambiguationData":[OSD([subQ45,subQ44,subQ43,subQ42,subQ41,subQ40,subQ39,subQ38,subQ37,subQ36,subQ35,subQ34,subQ33,subQ32,subQ31,subQ30,subQ29,subQ28,subQ27,subQ26,subQ25,subQ24,subQ23,subQ22,subQ21,subQ20,subQ19,subQ18,subQ17,subQ16,subQ15,subQ14,subQ13,subQ12,subQ11,subQ10,subQ9,subQ8,subQ7,subQ6,subQ5,subQ4,subQ3,subQ2,subQ1,subQ0])],"isStart":false})]}),makeQuery(id+"FZtU8A5xYbT4ezZ_1.1.FbB5umPfR1j8SLP_1.1.F8.opExtrude","CAP_FACE",FACE,{"disambiguationData":[OSD([subQ45,subQ44,subQ43,subQ42,subQ41,subQ40,subQ39,subQ38,subQ37,subQ36,subQ35,subQ34,subQ33,subQ32,subQ31,subQ30,subQ29,subQ28,subQ27,subQ26,subQ25,subQ24,subQ23,subQ22,subQ21,subQ20,subQ19,subQ18,subQ17,subQ16,subQ15,subQ14,subQ13,subQ12,subQ11,subQ10,subQ9,subQ8,subQ7,subQ6,subQ5,subQ4,subQ3,subQ2,subQ1,subQ0])],"isStart":false})]}),makeQuery(id+"FZtU8A5xYbT4ezZ_1.1.FbB5umPfR1j8SLP_1.2.F8.opExtrude","CAP_FACE",FACE,{"disambiguationData":[OSD([subQ45,subQ44,subQ43,subQ42,subQ41,subQ40,subQ39,subQ38,subQ37,subQ36,subQ35,subQ34,subQ33,subQ32,subQ31,subQ30,subQ29,subQ28,subQ27,subQ26,subQ25,subQ24,subQ23,subQ22,subQ21,subQ20,subQ19,subQ18,subQ17,subQ16,subQ15,subQ14,subQ13,subQ12,subQ11,subQ10,subQ9,subQ8,subQ7,subQ6,subQ5,subQ4,subQ3,subQ2,subQ1,subQ0])],"isStart":false})]}),makeQuery(id+"FZtU8A5xYbT4ezZ_1.1.FbB5umPfR1j8SLP_1.3.F8.opExtrude","CAP_FACE",FACE,{"disambiguationData":[OSD([subQ45,subQ44,subQ43,subQ42,subQ41,subQ40,subQ39,subQ38,subQ37,subQ36,subQ35,subQ34,subQ33,subQ32,subQ31,subQ30,subQ29,subQ28,subQ27,subQ26,subQ25,subQ24,subQ23,subQ22,subQ21,subQ20,subQ19,subQ18,subQ17,subQ16,subQ15,subQ14,subQ13,subQ12,subQ11,subQ10,subQ9,subQ8,subQ7,subQ6,subQ5,subQ4,subQ3,subQ2,subQ1,subQ0])],"isStart":false})]}),makeQuery(id+"FZtU8A5xYbT4ezZ_1.1.FbB5umPfR1j8SLP_1.4.F8.opExtrude","CAP_FACE",FACE,{"disambiguationData":[OSD([subQ45,subQ44,subQ43,subQ42,subQ41,subQ40,subQ39,subQ38,subQ37,subQ36,subQ35,subQ34,subQ33,subQ32,subQ31,subQ30,subQ29,subQ28,subQ27,subQ26,subQ25,subQ24,subQ23,subQ22,subQ21,subQ20,subQ19,subQ18,subQ17,subQ16,subQ15,subQ14,subQ13,subQ12,subQ11,subQ10,subQ9,subQ8,subQ7,subQ6,subQ5,subQ4,subQ3,subQ2,subQ1,subQ0])],"isStart":false})]}),makeQuery(id+"FZtU8A5xYbT4ezZ_1.1.FbB5umPfR1j8SLP_1.5.F8.opExtrude","CAP_FACE",FACE,{"disambiguationData":[OSD([subQ45,subQ44,subQ43,subQ42,subQ41,subQ40,subQ39,subQ38,subQ37,subQ36,subQ35,subQ34,subQ33,subQ32,subQ31,subQ30,subQ29,subQ28,subQ27,subQ26,subQ25,subQ24,subQ23,subQ22,subQ21,subQ20,subQ19,subQ18,subQ17,subQ16,subQ15,subQ14,subQ13,subQ12,subQ11,subQ10,subQ9,subQ8,subQ7,subQ6,subQ5,subQ4,subQ3,subQ2,subQ1,subQ0])],"isStart":false})]}),makeQuery(id+"FArHMtP67R58qOK_1.1.F8.opExtrude","CAP_FACE",FACE,{"disambiguationData":[OSD([subQ45,subQ44,subQ43,subQ42,subQ41,subQ40,subQ39,subQ38,subQ37,subQ36,subQ35,subQ34,subQ33,subQ32,subQ31,subQ30,subQ29,subQ28,subQ27,subQ26,subQ25,subQ24,subQ23,subQ22,subQ21,subQ20,subQ19,subQ18,subQ17,subQ16,subQ15,subQ14,subQ13,subQ12,subQ11,subQ10,subQ9,subQ8,subQ7,subQ6,subQ5,subQ4,subQ3,subQ2,subQ1,subQ0])],"isStart":false})]}),makeQuery(id+"FArHMtP67R58qOK_1.1.FbB5umPfR1j8SLP_1.1.F8.opExtrude","CAP_FACE",FACE,{"disambiguationData":[OSD([subQ45,subQ44,subQ43,subQ42,subQ41,subQ40,subQ39,subQ38,subQ37,subQ36,subQ35,subQ34,subQ33,subQ32,subQ31,subQ30,subQ29,subQ28,subQ27,subQ26,subQ25,subQ24,subQ23,subQ22,subQ21,subQ20,subQ19,subQ18,subQ17,subQ16,subQ15,subQ14,subQ13,subQ12,subQ11,subQ10,subQ9,subQ8,subQ7,subQ6,subQ5,subQ4,subQ3,subQ2,subQ1,subQ0])],"isStart":false})]}),makeQuery(id+"FArHMtP67R58qOK_1.1.FbB5umPfR1j8SLP_1.2.F8.opExtrude","CAP_FACE",FACE,{"disambiguationData":[OSD([subQ45,subQ44,subQ43,subQ42,subQ41,subQ40,subQ39,subQ38,subQ37,subQ36,subQ35,subQ34,subQ33,subQ32,subQ31,subQ30,subQ29,subQ28,subQ27,subQ26,subQ25,subQ24,subQ23,subQ22,subQ21,subQ20,subQ19,subQ18,subQ17,subQ16,subQ15,subQ14,subQ13,subQ12,subQ11,subQ10,subQ9,subQ8,subQ7,subQ6,subQ5,subQ4,subQ3,subQ2,subQ1,subQ0])],"isStart":false})]}),makeQuery(id+"FArHMtP67R58qOK_1.1.FbB5umPfR1j8SLP_1.3.F8.opExtrude","CAP_FACE",FACE,{"disambiguationData":[OSD([subQ45,subQ44,subQ43,subQ42,subQ41,subQ40,subQ39,subQ38,subQ37,subQ36,subQ35,subQ34,subQ33,subQ32,subQ31,subQ30,subQ29,subQ28,subQ27,subQ26,subQ25,subQ24,subQ23,subQ22,subQ21,subQ20,subQ19,subQ18,subQ17,subQ16,subQ15,subQ14,subQ13,subQ12,subQ11,subQ10,subQ9,subQ8,subQ7,subQ6,subQ5,subQ4,subQ3,subQ2,subQ1,subQ0])],"isStart":false})]}),makeQuery(id+"FArHMtP67R58qOK_1.1.FbB5umPfR1j8SLP_1.4.F8.opExtrude","CAP_FACE",FACE,{"disambiguationData":[OSD([subQ45,subQ44,subQ43,subQ42,subQ41,subQ40,subQ39,subQ38,subQ37,subQ36,subQ35,subQ34,subQ33,subQ32,subQ31,subQ30,subQ29,subQ28,subQ27,subQ26,subQ25,subQ24,subQ23,subQ22,subQ21,subQ20,subQ19,subQ18,subQ17,subQ16,subQ15,subQ14,subQ13,subQ12,subQ11,subQ10,subQ9,subQ8,subQ7,subQ6,subQ5,subQ4,subQ3,subQ2,subQ1,subQ0])],"isStart":false})]}),makeQuery(id+"FArHMtP67R58qOK_1.1.FbB5umPfR1j8SLP_1.5.F8.opExtrude","CAP_FACE",FACE,{"disambiguationData":[OSD([subQ45,subQ44,subQ43,subQ42,subQ41,subQ40,subQ39,subQ38,subQ37,subQ36,subQ35,subQ34,subQ33,subQ32,subQ31,subQ30,subQ29,subQ28,subQ27,subQ26,subQ25,subQ24,subQ23,subQ22,subQ21,subQ20,subQ19,subQ18,subQ17,subQ16,subQ15,subQ14,subQ13,subQ12,subQ11,subQ10,subQ9,subQ8,subQ7,subQ6,subQ5,subQ4,subQ3,subQ2,subQ1,subQ0])],"isStart":false})]});}
            extrude(context, id + "F10", {"entities" : qUnion([Q0]), "operationType" : NewBodyOperationType.REMOVE, "endBound" : BoundingType.UP_TO_SURFACE, "oppositeDirection" : true, "endBoundEntityFace" : qUnion([Q1]), "depth" : 25.4 * mm});
        }
        {
            var Q0;
            Q0=makeQuery(id+"F6.boolean.opBoolean","COPY",FACE,{"derivedFrom":makeQuery(id+"F6.opExtrude","SWEPT_FACE",FACE,{"disambiguationData":[OSD([sQuery(id+"F5.wireOp",EDGE,"E93.3.2")])]})});
            var Q1;
            Q1=makeQuery(id+"F8.boolean.opBoolean","SPLIT",FACE,{"disambiguationData":[TD([makeQuery(id+"F6.boolean.opBoolean","COPY",FACE,{"derivedFrom":makeQuery(id+"F6.opExtrude","SWEPT_FACE",FACE,{"disambiguationData":[OSD([sQuery(id+"F5.wireOp",EDGE,"E92.left")])]})})])],"derivedFrom":makeQuery(id+"F6.boolean.opBoolean","COPY",FACE,{"derivedFrom":makeQuery(id+"F6.opExtrude","SWEPT_FACE",FACE,{"disambiguationData":[OSD([sQuery(id+"F5.wireOp",EDGE,"E92.bottom")])]})})});
            cPlane(context, id + "F11", {"entities" : qUnion([Q0, Q1]), "cplaneType" : CPlaneType.MID_PLANE, "offset" : 25.4 * mm, "width" : 152.4 * mm, "height" : 152.4 * mm});
        }
        {
            var Q0;
            Q0=qCreatedBy(id+"F11.planeOp",FACE);
            var sketch = newSketch(context, id + "F12", { "sketchPlane" : qUnion([Q0])});
            skLineSegment(sketch, "E154", {"start": v(-217.77, -63.78) * mm, "end": v(-217.77, 3.18) * mm, "construction": true});
            skSolve(sketch);
        }
        {
            var Q0;
            Q0=makeQuery(id+"FYHNYUacGxg7GGj_1.5.F8.boolean.opBoolean","SPLIT",FACE,{"disambiguationData":[TD([makeQuery(id+"F6.boolean.opBoolean","COPY",FACE,{"derivedFrom":makeQuery(id+"F6.opExtrude","SWEPT_FACE",FACE,{"disambiguationData":[OSD([sQuery(id+"F5.wireOp",EDGE,"E93.5.1")])]})})])],"derivedFrom":makeQuery(id+"F6.boolean.opBoolean","COPY",FACE,{"derivedFrom":makeQuery(id+"F6.opExtrude","SWEPT_FACE",FACE,{"disambiguationData":[OSD([sQuery(id+"F5.wireOp",EDGE,"E93.5.0")])]})})});
            var Q1;
            Q1=makeQuery(id+"F6.boolean.opBoolean","COPY",FACE,{"derivedFrom":makeQuery(id+"F6.opExtrude","SWEPT_FACE",FACE,{"disambiguationData":[OSD([sQuery(id+"F5.wireOp",EDGE,"E124.MirrorCS")])]})});
            cPlane(context, id + "F13", {"entities" : qUnion([Q0, Q1]), "cplaneType" : CPlaneType.MID_PLANE, "offset" : 25.4 * mm, "width" : 152.4 * mm, "height" : 152.4 * mm});
        }
    });
